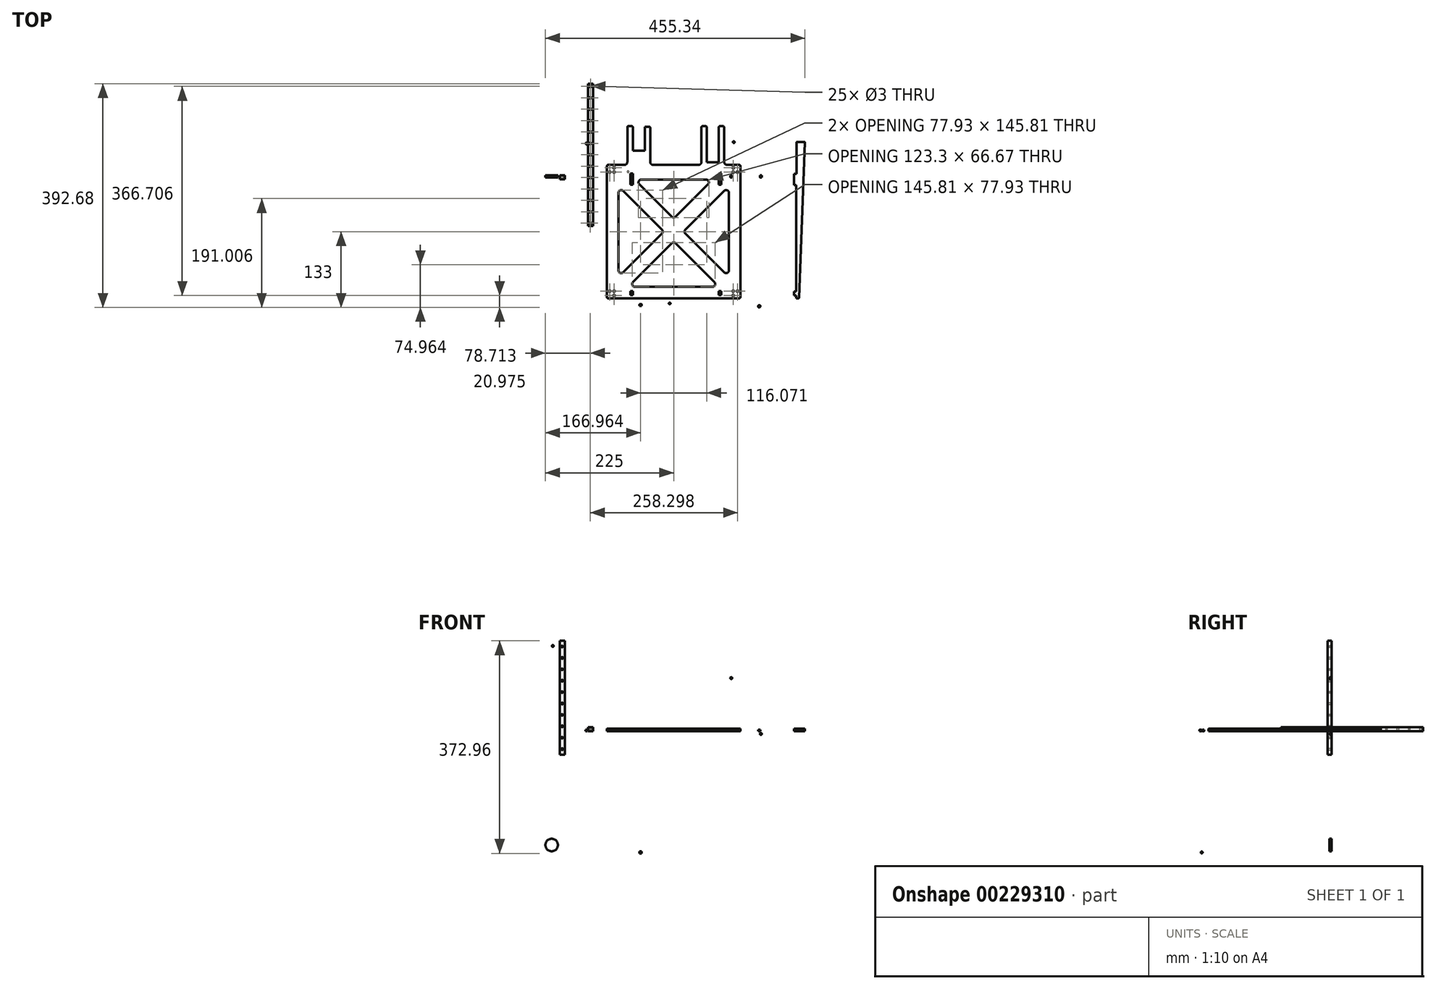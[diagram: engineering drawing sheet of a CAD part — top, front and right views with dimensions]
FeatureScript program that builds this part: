
annotation { "Feature Type Name" : "Feature", "Feature Type Description" : "" }
export const myFeature = defineFeature(function(context is Context, id is Id, definition is map)
    precondition{}
    {
        {
            var Q0;
            Q0=qCreatedBy(makeId("Top.planeOp"),FACE);
            var sketch = newSketch(context, id + "F0", { "sketchPlane" : qUnion([Q0])});
            skCircle(sketch, "E0", {"center": v(165.5, 58) * mm, "radius": 1.5 * mm});
            skCircle(sketch, "E1", {"center": v(-45.5, 91) * mm, "radius": 1.5 * mm});
            skCircle(sketch, "E2", {"center": v(210, 90) * mm, "radius": 2 * mm});
            skCircle(sketch, "E3", {"center": v(-93, 67) * mm, "radius": 1.5 * mm});
            skCircle(sketch, "E4", {"center": v(213, 67) * mm, "radius": 1.5 * mm});
            skCircle(sketch, "E5", {"center": v(210, 59) * mm, "radius": 2 * mm});
            skCircle(sketch, "E6", {"center": v(-81, -229) * mm, "radius": 2 * mm});
            skCircle(sketch, "E7", {"center": v(198, -220) * mm, "radius": 2 * mm});
            skCircle(sketch, "E8", {"center": v(-81, 78) * mm, "radius": 2 * mm});
            skCircle(sketch, "E9", {"center": v(198, 64) * mm, "radius": 2 * mm});
            skCircle(sketch, "E10", {"center": v(203, 47) * mm, "radius": 1.65 * mm});
            skCircle(sketch, "E11", {"center": v(203, 7) * mm, "radius": 1.65 * mm});
            skCircle(sketch, "E12", {"center": v(203, -173) * mm, "radius": 1.65 * mm});
            skCircle(sketch, "E13", {"center": v(-83, 47) * mm, "radius": 1.65 * mm});
            skCircle(sketch, "E14", {"center": v(-83, 7) * mm, "radius": 1.65 * mm});
            skCircle(sketch, "E15", {"center": v(-83, -173) * mm, "radius": 1.65 * mm});
            skCircle(sketch, "E16", {"center": v(-83, -193) * mm, "radius": 1.65 * mm});
            skCircle(sketch, "E17", {"center": v(-83, -153) * mm, "radius": 1.65 * mm});
            skCircle(sketch, "E18", {"center": v(-83, 27) * mm, "radius": 1.65 * mm});
            skCircle(sketch, "E19", {"center": v(203, -193) * mm, "radius": 1.65 * mm});
            skCircle(sketch, "E20", {"center": v(203, -153) * mm, "radius": 1.65 * mm});
            skCircle(sketch, "E21", {"center": v(203, 27) * mm, "radius": 1.65 * mm});
            skCircle(sketch, "E22", {"center": v(201, 78) * mm, "radius": 2 * mm});
            skCircle(sketch, "E23", {"center": v(-78, 64) * mm, "radius": 2 * mm});
            skCircle(sketch, "E24", {"center": v(201, -229) * mm, "radius": 2 * mm});
            skCircle(sketch, "E25", {"center": v(-78, -220) * mm, "radius": 2 * mm});
            skCircle(sketch, "E26", {"center": v(-90, 59) * mm, "radius": 2 * mm});
            skCircle(sketch, "E27", {"center": v(213, 81) * mm, "radius": 1.5 * mm});
            skCircle(sketch, "E28", {"center": v(-93, 81) * mm, "radius": 1.5 * mm});
            skCircle(sketch, "E29", {"center": v(-90, 90) * mm, "radius": 2 * mm});
            skCircle(sketch, "E30", {"center": v(-45.5, 58) * mm, "radius": 1.5 * mm});
            skCircle(sketch, "E31", {"center": v(165.5, 91) * mm, "radius": 1.5 * mm});
            skCircle(sketch, "E32", {"center": v(-93, -219) * mm, "radius": 1.5 * mm});
            skCircle(sketch, "E33", {"center": v(-93, -233) * mm, "radius": 1.5 * mm});
            skCircle(sketch, "E34", {"center": v(213, -233) * mm, "radius": 1.5 * mm});
            skCircle(sketch, "E35", {"center": v(213, -219) * mm, "radius": 1.5 * mm});
            skCircle(sketch, "E36", {"center": v(67, -225) * mm, "radius": 1.5 * mm});
            skCircle(sketch, "E37", {"center": v(53, -225) * mm, "radius": 1.5 * mm});
            skLineSegment(sketch, "E38", {"start": v(147.5, 57) * mm, "end": v(152.5, 57) * mm});
            skLineSegment(sketch, "E39", {"start": v(152.5, 61) * mm, "end": v(147.5, 61) * mm});
            skLineSegment(sketch, "E40", {"start": v(178.5, 88) * mm, "end": v(183.5, 88) * mm});
            skLineSegment(sketch, "E41", {"start": v(183.5, 92) * mm, "end": v(178.5, 92) * mm});
            skLineSegment(sketch, "E42", {"start": v(-58.5, 61) * mm, "end": v(-63.5, 61) * mm});
            skLineSegment(sketch, "E43", {"start": v(-63.5, 57) * mm, "end": v(-58.5, 57) * mm});
            skLineSegment(sketch, "E44", {"start": v(-27.5, 92) * mm, "end": v(-32.5, 92) * mm});
            skLineSegment(sketch, "E45", {"start": v(-32.5, 88) * mm, "end": v(-27.5, 88) * mm});
            skLineSegment(sketch, "E46", {"start": v(187, 49) * mm, "end": v(187, 53) * mm});
            skLineSegment(sketch, "E47", {"start": v(-67, 53) * mm, "end": v(-67, 49) * mm});
            skLineSegment(sketch, "E48", {"start": v(188, 95) * mm, "end": v(188, 91) * mm});
            skLineSegment(sketch, "E49", {"start": v(193, 86) * mm, "end": v(195, 86) * mm});
            skLineSegment(sketch, "E50", {"start": v(200, 91) * mm, "end": v(200, 95) * mm});
            skLineSegment(sketch, "E51", {"start": v(215, 96) * mm, "end": v(201, 96) * mm});
            skLineSegment(sketch, "E52", {"start": v(-80, 95) * mm, "end": v(-80, 91) * mm});
            skLineSegment(sketch, "E53", {"start": v(-75, 86) * mm, "end": v(-73, 86) * mm});
            skLineSegment(sketch, "E54", {"start": v(-68, 91) * mm, "end": v(-68, 95) * mm});
            skLineSegment(sketch, "E55", {"start": v(-58.5, 92) * mm, "end": v(-63.5, 92) * mm});
            skLineSegment(sketch, "E56", {"start": v(-63.5, 88) * mm, "end": v(-58.5, 88) * mm});
            skLineSegment(sketch, "E57", {"start": v(-27.5, 61) * mm, "end": v(-32.5, 61) * mm});
            skLineSegment(sketch, "E58", {"start": v(-32.5, 57) * mm, "end": v(-27.5, 57) * mm});
            skLineSegment(sketch, "E59", {"start": v(147.5, 88) * mm, "end": v(152.5, 88) * mm});
            skLineSegment(sketch, "E60", {"start": v(152.5, 92) * mm, "end": v(147.5, 92) * mm});
            skLineSegment(sketch, "E61", {"start": v(178.5, 57) * mm, "end": v(183.5, 57) * mm});
            skLineSegment(sketch, "E62", {"start": v(183.5, 61) * mm, "end": v(178.5, 61) * mm});
            skLineSegment(sketch, "E63", {"start": v(-81, 96) * mm, "end": v(-95, 96) * mm});
            skArc(sketch, "E64", {"start": v(152.5, 57) * mm, "mid": v(154.5, 59) * mm, "end": v(152.5, 61) * mm});
            skArc(sketch, "E65", {"start": v(147.5, 61) * mm, "mid": v(145.5, 59) * mm, "end": v(147.5, 57) * mm});
            skArc(sketch, "E66", {"start": v(183.5, 88) * mm, "mid": v(185.5, 90) * mm, "end": v(183.5, 92) * mm});
            skArc(sketch, "E67", {"start": v(178.5, 92) * mm, "mid": v(176.5, 90) * mm, "end": v(178.5, 88) * mm});
            skArc(sketch, "E68", {"start": v(-63.5, 61) * mm, "mid": v(-65.5, 59) * mm, "end": v(-63.5, 57) * mm});
            skArc(sketch, "E69", {"start": v(-58.5, 57) * mm, "mid": v(-56.5, 59) * mm, "end": v(-58.5, 61) * mm});
            skArc(sketch, "E70", {"start": v(-32.5, 92) * mm, "mid": v(-34.5, 90) * mm, "end": v(-32.5, 88) * mm});
            skArc(sketch, "E71", {"start": v(-27.5, 88) * mm, "mid": v(-25.5, 90) * mm, "end": v(-27.5, 92) * mm});
            skArc(sketch, "E72", {"start": v(195, 41) * mm, "mid": v(192.66, 46.66) * mm, "end": v(187, 49) * mm});
            skArc(sketch, "E73", {"start": v(-67, 49) * mm, "mid": v(-72.66, 46.66) * mm, "end": v(-75, 41) * mm});
            skArc(sketch, "E74", {"start": v(-75, -214) * mm, "mid": v(-72.66, -219.66) * mm, "end": v(-67, -222) * mm});
            skArc(sketch, "E75", {"start": v(187, -222) * mm, "mid": v(192.66, -219.66) * mm, "end": v(195, -214) * mm});
            skArc(sketch, "E76", {"start": v(188, 95) * mm, "mid": v(187.7, 95.7) * mm, "end": v(187, 96) * mm});
            skArc(sketch, "E77", {"start": v(188, 91) * mm, "mid": v(189.46, 87.46) * mm, "end": v(193, 86) * mm});
            skArc(sketch, "E78", {"start": v(195, 86) * mm, "mid": v(198.54, 87.46) * mm, "end": v(200, 91) * mm});
            skArc(sketch, "E79", {"start": v(201, 96) * mm, "mid": v(200.3, 95.7) * mm, "end": v(200, 95) * mm});
            skArc(sketch, "E80", {"start": v(216, 95) * mm, "mid": v(215.7, 95.7) * mm, "end": v(215, 96) * mm});
            skArc(sketch, "E81", {"start": v(215, -236) * mm, "mid": v(215.7, -235.7) * mm, "end": v(216, -235) * mm});
            skArc(sketch, "E82", {"start": v(-96, -235) * mm, "mid": v(-95.7, -235.7) * mm, "end": v(-95, -236) * mm});
            skArc(sketch, "E83", {"start": v(-95, 96) * mm, "mid": v(-95.7, 95.7) * mm, "end": v(-96, 95) * mm});
            skArc(sketch, "E84", {"start": v(-80, 95) * mm, "mid": v(-80.3, 95.7) * mm, "end": v(-81, 96) * mm});
            skArc(sketch, "E85", {"start": v(-80, 91) * mm, "mid": v(-78.54, 87.46) * mm, "end": v(-75, 86) * mm});
            skArc(sketch, "E86", {"start": v(-73, 86) * mm, "mid": v(-69.46, 87.46) * mm, "end": v(-68, 91) * mm});
            skArc(sketch, "E87", {"start": v(-67, 96) * mm, "mid": v(-67.7, 95.7) * mm, "end": v(-68, 95) * mm});
            skArc(sketch, "E88", {"start": v(-63.5, 92) * mm, "mid": v(-65.5, 90) * mm, "end": v(-63.5, 88) * mm});
            skArc(sketch, "E89", {"start": v(-58.5, 88) * mm, "mid": v(-56.5, 90) * mm, "end": v(-58.5, 92) * mm});
            skArc(sketch, "E90", {"start": v(-32.5, 61) * mm, "mid": v(-34.5, 59) * mm, "end": v(-32.5, 57) * mm});
            skArc(sketch, "E91", {"start": v(-27.5, 57) * mm, "mid": v(-25.5, 59) * mm, "end": v(-27.5, 61) * mm});
            skArc(sketch, "E92", {"start": v(152.5, 88) * mm, "mid": v(154.5, 90) * mm, "end": v(152.5, 92) * mm});
            skArc(sketch, "E93", {"start": v(147.5, 92) * mm, "mid": v(145.5, 90) * mm, "end": v(147.5, 88) * mm});
            skArc(sketch, "E94", {"start": v(183.5, 57) * mm, "mid": v(185.5, 59) * mm, "end": v(183.5, 61) * mm});
            skArc(sketch, "E95", {"start": v(178.5, 61) * mm, "mid": v(176.5, 59) * mm, "end": v(178.5, 57) * mm});
            skLineSegment(sketch, "E96", {"start": v(-67, 96) * mm, "end": v(187, 96) * mm});
            skLineSegment(sketch, "E97", {"start": v(-67, 53) * mm, "end": v(187, 53) * mm});
            skLineSegment(sketch, "E98", {"start": v(216, 95) * mm, "end": v(216, -235) * mm});
            skLineSegment(sketch, "E99", {"start": v(195, 41) * mm, "end": v(195, -214) * mm});
            skLineSegment(sketch, "E100", {"start": v(187, -222) * mm, "end": v(-67, -222) * mm});
            skLineSegment(sketch, "E101", {"start": v(215, -236) * mm, "end": v(-95, -236) * mm});
            skLineSegment(sketch, "E102", {"start": v(-96, -235) * mm, "end": v(-96, 95) * mm});
            skLineSegment(sketch, "E103", {"start": v(-75, 41) * mm, "end": v(-75, -214) * mm});
            skCircle(sketch, "E104", {"center": v(203, -133) * mm, "radius": 1.5 * mm});
            skCircle(sketch, "E105", {"center": v(203, -113) * mm, "radius": 1.5 * mm});
            skCircle(sketch, "E106", {"center": v(203, -93) * mm, "radius": 1.5 * mm});
            skCircle(sketch, "E107", {"center": v(203, -73) * mm, "radius": 1.5 * mm});
            skCircle(sketch, "E108", {"center": v(203, -53) * mm, "radius": 1.5 * mm});
            skCircle(sketch, "E109", {"center": v(203, -33) * mm, "radius": 1.5 * mm});
            skCircle(sketch, "E110", {"center": v(203, -13) * mm, "radius": 1.85 * mm});
            skCircle(sketch, "E111", {"center": v(-83, -113) * mm, "radius": 1.5 * mm});
            skCircle(sketch, "E112", {"center": v(-83, -133) * mm, "radius": 1.5 * mm});
            skCircle(sketch, "E113", {"center": v(-83, -93) * mm, "radius": 1.5 * mm});
            skCircle(sketch, "E114", {"center": v(-83, -73) * mm, "radius": 1.5 * mm});
            skCircle(sketch, "E115", {"center": v(-83, -53) * mm, "radius": 1.5 * mm});
            skCircle(sketch, "E116", {"center": v(-83, -33) * mm, "radius": 1.5 * mm});
            skCircle(sketch, "E117", {"center": v(-83, -13) * mm, "radius": 1.5 * mm});
            skSolve(sketch);
        }
        {
            var Q0;
            Q0=qCreatedBy(makeId("Top.planeOp"),FACE);
            var sketch = newSketch(context, id + "F1", { "sketchPlane" : qUnion([Q0])});
            skCircle(sketch, "E118", {"center": v(-20, 6.05) * mm, "radius": 1.5 * mm});
            skCircle(sketch, "E119", {"center": v(140, 6.05) * mm, "radius": 1.5 * mm});
            skCircle(sketch, "E120", {"center": v(195.5, 1) * mm, "radius": 1.65 * mm});
            skCircle(sketch, "E121", {"center": v(210.5, 11) * mm, "radius": 1.65 * mm});
            skCircle(sketch, "E122", {"center": v(180, 6) * mm, "radius": 1.5 * mm});
            skCircle(sketch, "E123", {"center": v(194, 18) * mm, "radius": 1.65 * mm});
            skCircle(sketch, "E124", {"center": v(194, -6) * mm, "radius": 1.65 * mm});
            skCircle(sketch, "E125", {"center": v(-92, -6) * mm, "radius": 1.65 * mm});
            skCircle(sketch, "E126", {"center": v(-92, 18) * mm, "radius": 1.65 * mm});
            skCircle(sketch, "E127", {"center": v(-40, 6) * mm, "radius": 1.5 * mm});
            skCircle(sketch, "E128", {"center": v(-78, 6) * mm, "radius": 1.5 * mm});
            skCircle(sketch, "E129", {"center": v(-90.5, 1) * mm, "radius": 1.65 * mm});
            skCircle(sketch, "E130", {"center": v(-75.5, 11) * mm, "radius": 1.65 * mm});
            skCircle(sketch, "E131", {"center": v(-75.5, 1) * mm, "radius": 1.65 * mm});
            skCircle(sketch, "E132", {"center": v(-90.5, 11) * mm, "radius": 1.65 * mm});
            skCircle(sketch, "E133", {"center": v(-60, 6) * mm, "radius": 1.5 * mm});
            skCircle(sketch, "E134", {"center": v(-74, 18) * mm, "radius": 1.65 * mm});
            skCircle(sketch, "E135", {"center": v(-74, -6) * mm, "radius": 1.65 * mm});
            skCircle(sketch, "E136", {"center": v(212, -6) * mm, "radius": 1.65 * mm});
            skCircle(sketch, "E137", {"center": v(212, 18) * mm, "radius": 1.65 * mm});
            skCircle(sketch, "E138", {"center": v(160, 6) * mm, "radius": 1.5 * mm});
            skCircle(sketch, "E139", {"center": v(198, 6) * mm, "radius": 1.5 * mm});
            skCircle(sketch, "E140", {"center": v(210.5, 1) * mm, "radius": 1.65 * mm});
            skCircle(sketch, "E141", {"center": v(195.5, 11) * mm, "radius": 1.65 * mm});
            skCircle(sketch, "E142", {"center": v(0, 6.05) * mm, "radius": 1.5 * mm});
            skLineSegment(sketch, "E143", {"start": v(193, -10) * mm, "end": v(213, -10) * mm});
            skLineSegment(sketch, "E144", {"start": v(191, -0.5) * mm, "end": v(191, -8) * mm});
            skLineSegment(sketch, "E145", {"start": v(-71, -8) * mm, "end": v(-71, -0.5) * mm});
            skLineSegment(sketch, "E146", {"start": v(-93, -10) * mm, "end": v(-73, -10) * mm});
            skLineSegment(sketch, "E147", {"start": v(-95, 20) * mm, "end": v(-95, -8) * mm});
            skLineSegment(sketch, "E148", {"start": v(-73, 22) * mm, "end": v(-93, 22) * mm});
            skLineSegment(sketch, "E149", {"start": v(-71, 12.5) * mm, "end": v(-71, 20) * mm});
            skLineSegment(sketch, "E150", {"start": v(191, 20) * mm, "end": v(191, 12.5) * mm});
            skLineSegment(sketch, "E151", {"start": v(213, 22) * mm, "end": v(193, 22) * mm});
            skLineSegment(sketch, "E152", {"start": v(215, -8) * mm, "end": v(215, 20) * mm});
            skArc(sketch, "E153", {"start": v(213, -10) * mm, "mid": v(214.41, -9.41) * mm, "end": v(215, -8) * mm});
            skArc(sketch, "E154", {"start": v(191, -8) * mm, "mid": v(191.59, -9.41) * mm, "end": v(193, -10) * mm});
            skArc(sketch, "E155", {"start": v(191, -0.5) * mm, "mid": v(190.41, 0.91) * mm, "end": v(189, 1.5) * mm});
            skArc(sketch, "E156", {"start": v(-69, 1.5) * mm, "mid": v(-70.41, 0.91) * mm, "end": v(-71, -0.5) * mm});
            skArc(sketch, "E157", {"start": v(-73, -10) * mm, "mid": v(-71.59, -9.41) * mm, "end": v(-71, -8) * mm});
            skArc(sketch, "E158", {"start": v(-95, -8) * mm, "mid": v(-94.41, -9.41) * mm, "end": v(-93, -10) * mm});
            skArc(sketch, "E159", {"start": v(-93, 22) * mm, "mid": v(-94.41, 21.41) * mm, "end": v(-95, 20) * mm});
            skArc(sketch, "E160", {"start": v(-71, 20) * mm, "mid": v(-71.59, 21.41) * mm, "end": v(-73, 22) * mm});
            skArc(sketch, "E161", {"start": v(-71, 12.5) * mm, "mid": v(-70.41, 11.09) * mm, "end": v(-69, 10.5) * mm});
            skArc(sketch, "E162", {"start": v(189, 10.5) * mm, "mid": v(190.41, 11.09) * mm, "end": v(191, 12.5) * mm});
            skArc(sketch, "E163", {"start": v(193, 22) * mm, "mid": v(191.59, 21.41) * mm, "end": v(191, 20) * mm});
            skArc(sketch, "E164", {"start": v(215, 20) * mm, "mid": v(214.41, 21.41) * mm, "end": v(213, 22) * mm});
            skLineSegment(sketch, "E165", {"start": v(-69, 10.5) * mm, "end": v(189, 10.5) * mm});
            skLineSegment(sketch, "E166", {"start": v(189, 1.5) * mm, "end": v(-69, 1.5) * mm});
            skCircle(sketch, "E167", {"center": v(20, 6.05) * mm, "radius": 1.5 * mm});
            skCircle(sketch, "E168", {"center": v(40, 6.05) * mm, "radius": 1.5 * mm});
            skCircle(sketch, "E169", {"center": v(60, 6.05) * mm, "radius": 1.5 * mm});
            skCircle(sketch, "E170", {"center": v(120, 6.05) * mm, "radius": 1.5 * mm});
            skCircle(sketch, "E171", {"center": v(80, 6.05) * mm, "radius": 1.5 * mm});
            skCircle(sketch, "E172", {"center": v(100, 6.05) * mm, "radius": 1.5 * mm});
            skSolve(sketch);
        }
        {
            var Q0;
            Q0=makeQuery(id+"F0.imprint","IMPRINT",FACE,{"disambiguationData":[TD([[makeQuery(id+"F0.imprint","IMPRINT",EDGE,{"derivedFrom":sQuery(id+"F0.wireOp",EDGE,"E0")}),1.0]])]});
            extrude(context, id + "F2", {"entities" : qUnion([Q0]), "depth" : 2 * mm});
        }
        {
            var Q0;
            Q0=makeQuery(id+"F1.imprint","IMPRINT",FACE,{"disambiguationData":[TD([[makeQuery(id+"F1.imprint","IMPRINT",EDGE,{"derivedFrom":sQuery(id+"F1.wireOp",EDGE,"E118")}),1.0]])]});
            extrude(context, id + "F3", {"entities" : qUnion([Q0]), "depth" : 2 * mm});
        }
        {
            var Q0;
            Q0=qCreatedBy(makeId("Top.planeOp"),FACE);
            var sketch = newSketch(context, id + "F4", { "sketchPlane" : qUnion([Q0])});
            skCircle(sketch, "E173", {"center": v(53, -225) * mm, "radius": 1.5 * mm});
            skCircle(sketch, "E174", {"center": v(-90, 59) * mm, "radius": 2 * mm});
            skCircle(sketch, "E175", {"center": v(-81, -229) * mm, "radius": 2 * mm});
            skCircle(sketch, "E176", {"center": v(198, -220) * mm, "radius": 2 * mm});
            skCircle(sketch, "E177", {"center": v(-81, 78) * mm, "radius": 2 * mm});
            skCircle(sketch, "E178", {"center": v(198, 64) * mm, "radius": 2 * mm});
            skCircle(sketch, "E179", {"center": v(75.5, 90) * mm, "radius": 2 * mm});
            skCircle(sketch, "E180", {"center": v(44.5, 59) * mm, "radius": 2 * mm});
            skCircle(sketch, "E181", {"center": v(75.5, 59) * mm, "radius": 2 * mm});
            skCircle(sketch, "E182", {"center": v(44.5, 90) * mm, "radius": 2 * mm});
            skCircle(sketch, "E183", {"center": v(60, 74.5) * mm, "radius": 11.75 * mm});
            skCircle(sketch, "E184", {"center": v(201, 78) * mm, "radius": 2 * mm});
            skCircle(sketch, "E185", {"center": v(-78, 64) * mm, "radius": 2 * mm});
            skCircle(sketch, "E186", {"center": v(201, -229) * mm, "radius": 2 * mm});
            skCircle(sketch, "E187", {"center": v(-78, -220) * mm, "radius": 2 * mm});
            skCircle(sketch, "E188", {"center": v(210, 59) * mm, "radius": 2 * mm});
            skCircle(sketch, "E189", {"center": v(67, -225) * mm, "radius": 1.5 * mm});
            skCircle(sketch, "E190", {"center": v(-93, -219) * mm, "radius": 1.5 * mm});
            skCircle(sketch, "E191", {"center": v(-93, -233) * mm, "radius": 1.5 * mm});
            skCircle(sketch, "E192", {"center": v(213, -233) * mm, "radius": 1.5 * mm});
            skCircle(sketch, "E193", {"center": v(213, -219) * mm, "radius": 1.5 * mm});
            skCircle(sketch, "E194", {"center": v(213, 81) * mm, "radius": 1.5 * mm});
            skCircle(sketch, "E195", {"center": v(213, 67) * mm, "radius": 1.5 * mm});
            skCircle(sketch, "E196", {"center": v(-93, 81) * mm, "radius": 1.5 * mm});
            skCircle(sketch, "E197", {"center": v(-93, 67) * mm, "radius": 1.5 * mm});
            skLineSegment(sketch, "E198", {"start": v(187, 49) * mm, "end": v(187, 53) * mm});
            skLineSegment(sketch, "E199", {"start": v(-67, 53) * mm, "end": v(-67, 49) * mm});
            skLineSegment(sketch, "E200", {"start": v(163, 62.75) * mm, "end": v(168, 62.75) * mm});
            skLineSegment(sketch, "E201", {"start": v(168, 86.25) * mm, "end": v(163, 86.25) * mm});
            skLineSegment(sketch, "E202", {"start": v(147.5, 88) * mm, "end": v(152.5, 88) * mm});
            skLineSegment(sketch, "E203", {"start": v(152.5, 92) * mm, "end": v(147.5, 92) * mm});
            skLineSegment(sketch, "E204", {"start": v(178.5, 57) * mm, "end": v(183.5, 57) * mm});
            skLineSegment(sketch, "E205", {"start": v(183.5, 61) * mm, "end": v(178.5, 61) * mm});
            skLineSegment(sketch, "E206", {"start": v(-27.5, 61) * mm, "end": v(-32.5, 61) * mm});
            skLineSegment(sketch, "E207", {"start": v(-32.5, 57) * mm, "end": v(-27.5, 57) * mm});
            skLineSegment(sketch, "E208", {"start": v(-58.5, 92) * mm, "end": v(-63.5, 92) * mm});
            skLineSegment(sketch, "E209", {"start": v(-63.5, 88) * mm, "end": v(-58.5, 88) * mm});
            skLineSegment(sketch, "E210", {"start": v(-84, 84) * mm, "end": v(-95, 84) * mm});
            skLineSegment(sketch, "E211", {"start": v(-84, 95) * mm, "end": v(-84, 84) * mm});
            skLineSegment(sketch, "E212", {"start": v(-80, 95) * mm, "end": v(-80, 91) * mm});
            skLineSegment(sketch, "E213", {"start": v(-75, 86) * mm, "end": v(-73, 86) * mm});
            skLineSegment(sketch, "E214", {"start": v(-68, 91) * mm, "end": v(-68, 95) * mm});
            skLineSegment(sketch, "E215", {"start": v(188, 95) * mm, "end": v(188, 91) * mm});
            skLineSegment(sketch, "E216", {"start": v(193, 86) * mm, "end": v(195, 86) * mm});
            skLineSegment(sketch, "E217", {"start": v(200, 91) * mm, "end": v(200, 95) * mm});
            skLineSegment(sketch, "E218", {"start": v(203, 96) * mm, "end": v(201, 96) * mm});
            skLineSegment(sketch, "E219", {"start": v(204, 84) * mm, "end": v(204, 95) * mm});
            skLineSegment(sketch, "E220", {"start": v(215, 84) * mm, "end": v(204, 84) * mm});
            skLineSegment(sketch, "E221", {"start": v(-43, 86.25) * mm, "end": v(-48, 86.25) * mm});
            skLineSegment(sketch, "E222", {"start": v(-48, 62.75) * mm, "end": v(-43, 62.75) * mm});
            skLineSegment(sketch, "E223", {"start": v(-27.5, 92) * mm, "end": v(-32.5, 92) * mm});
            skLineSegment(sketch, "E224", {"start": v(-32.5, 88) * mm, "end": v(-27.5, 88) * mm});
            skLineSegment(sketch, "E225", {"start": v(-58.5, 61) * mm, "end": v(-63.5, 61) * mm});
            skLineSegment(sketch, "E226", {"start": v(-63.5, 57) * mm, "end": v(-58.5, 57) * mm});
            skLineSegment(sketch, "E227", {"start": v(147.5, 57) * mm, "end": v(152.5, 57) * mm});
            skLineSegment(sketch, "E228", {"start": v(152.5, 61) * mm, "end": v(147.5, 61) * mm});
            skLineSegment(sketch, "E229", {"start": v(178.5, 88) * mm, "end": v(183.5, 88) * mm});
            skLineSegment(sketch, "E230", {"start": v(183.5, 92) * mm, "end": v(178.5, 92) * mm});
            skLineSegment(sketch, "E231", {"start": v(-81, 96) * mm, "end": v(-83, 96) * mm});
            skArc(sketch, "E232", {"start": v(195, 41) * mm, "mid": v(192.66, 46.66) * mm, "end": v(187, 49) * mm});
            skArc(sketch, "E233", {"start": v(-67, 49) * mm, "mid": v(-72.66, 46.66) * mm, "end": v(-75, 41) * mm});
            skArc(sketch, "E234", {"start": v(-75, -214) * mm, "mid": v(-72.66, -219.66) * mm, "end": v(-67, -222) * mm});
            skArc(sketch, "E235", {"start": v(187, -222) * mm, "mid": v(192.66, -219.66) * mm, "end": v(195, -214) * mm});
            skArc(sketch, "E236", {"start": v(168, 62.75) * mm, "mid": v(179.75, 74.5) * mm, "end": v(168, 86.25) * mm});
            skArc(sketch, "E237", {"start": v(163, 86.25) * mm, "mid": v(151.25, 74.5) * mm, "end": v(163, 62.75) * mm});
            skArc(sketch, "E238", {"start": v(152.5, 88) * mm, "mid": v(154.5, 90) * mm, "end": v(152.5, 92) * mm});
            skArc(sketch, "E239", {"start": v(147.5, 92) * mm, "mid": v(145.5, 90) * mm, "end": v(147.5, 88) * mm});
            skArc(sketch, "E240", {"start": v(183.5, 57) * mm, "mid": v(185.5, 59) * mm, "end": v(183.5, 61) * mm});
            skArc(sketch, "E241", {"start": v(178.5, 61) * mm, "mid": v(176.5, 59) * mm, "end": v(178.5, 57) * mm});
            skArc(sketch, "E242", {"start": v(-32.5, 61) * mm, "mid": v(-34.5, 59) * mm, "end": v(-32.5, 57) * mm});
            skArc(sketch, "E243", {"start": v(-27.5, 57) * mm, "mid": v(-25.5, 59) * mm, "end": v(-27.5, 61) * mm});
            skArc(sketch, "E244", {"start": v(-63.5, 92) * mm, "mid": v(-65.5, 90) * mm, "end": v(-63.5, 88) * mm});
            skArc(sketch, "E245", {"start": v(-58.5, 88) * mm, "mid": v(-56.5, 90) * mm, "end": v(-58.5, 92) * mm});
            skArc(sketch, "E246", {"start": v(-95, 84) * mm, "mid": v(-95.7, 83.7) * mm, "end": v(-96, 83) * mm});
            skArc(sketch, "E247", {"start": v(-83, 96) * mm, "mid": v(-83.7, 95.7) * mm, "end": v(-84, 95) * mm});
            skArc(sketch, "E248", {"start": v(-80, 95) * mm, "mid": v(-80.3, 95.7) * mm, "end": v(-81, 96) * mm});
            skArc(sketch, "E249", {"start": v(-80, 91) * mm, "mid": v(-78.54, 87.46) * mm, "end": v(-75, 86) * mm});
            skArc(sketch, "E250", {"start": v(-73, 86) * mm, "mid": v(-69.46, 87.46) * mm, "end": v(-68, 91) * mm});
            skArc(sketch, "E251", {"start": v(-67, 96) * mm, "mid": v(-67.7, 95.7) * mm, "end": v(-68, 95) * mm});
            skArc(sketch, "E252", {"start": v(188, 95) * mm, "mid": v(187.7, 95.7) * mm, "end": v(187, 96) * mm});
            skArc(sketch, "E253", {"start": v(188, 91) * mm, "mid": v(189.46, 87.46) * mm, "end": v(193, 86) * mm});
            skArc(sketch, "E254", {"start": v(195, 86) * mm, "mid": v(198.54, 87.46) * mm, "end": v(200, 91) * mm});
            skArc(sketch, "E255", {"start": v(201, 96) * mm, "mid": v(200.3, 95.7) * mm, "end": v(200, 95) * mm});
            skArc(sketch, "E256", {"start": v(204, 95) * mm, "mid": v(203.7, 95.7) * mm, "end": v(203, 96) * mm});
            skArc(sketch, "E257", {"start": v(216, 83) * mm, "mid": v(215.7, 83.7) * mm, "end": v(215, 84) * mm});
            skArc(sketch, "E258", {"start": v(215, -236) * mm, "mid": v(215.7, -235.7) * mm, "end": v(216, -235) * mm});
            skArc(sketch, "E259", {"start": v(-96, -235) * mm, "mid": v(-95.7, -235.7) * mm, "end": v(-95, -236) * mm});
            skArc(sketch, "E260", {"start": v(-48, 86.25) * mm, "mid": v(-59.75, 74.5) * mm, "end": v(-48, 62.75) * mm});
            skArc(sketch, "E261", {"start": v(-43, 62.75) * mm, "mid": v(-31.25, 74.5) * mm, "end": v(-43, 86.25) * mm});
            skArc(sketch, "E262", {"start": v(-32.5, 92) * mm, "mid": v(-34.5, 90) * mm, "end": v(-32.5, 88) * mm});
            skArc(sketch, "E263", {"start": v(-27.5, 88) * mm, "mid": v(-25.5, 90) * mm, "end": v(-27.5, 92) * mm});
            skArc(sketch, "E264", {"start": v(-63.5, 61) * mm, "mid": v(-65.5, 59) * mm, "end": v(-63.5, 57) * mm});
            skArc(sketch, "E265", {"start": v(-58.5, 57) * mm, "mid": v(-56.5, 59) * mm, "end": v(-58.5, 61) * mm});
            skArc(sketch, "E266", {"start": v(152.5, 57) * mm, "mid": v(154.5, 59) * mm, "end": v(152.5, 61) * mm});
            skArc(sketch, "E267", {"start": v(147.5, 61) * mm, "mid": v(145.5, 59) * mm, "end": v(147.5, 57) * mm});
            skArc(sketch, "E268", {"start": v(183.5, 88) * mm, "mid": v(185.5, 90) * mm, "end": v(183.5, 92) * mm});
            skArc(sketch, "E269", {"start": v(178.5, 92) * mm, "mid": v(176.5, 90) * mm, "end": v(178.5, 88) * mm});
            skLineSegment(sketch, "E270", {"start": v(-67, 96) * mm, "end": v(187, 96) * mm});
            skLineSegment(sketch, "E271", {"start": v(216, 83) * mm, "end": v(216, -235) * mm});
            skLineSegment(sketch, "E272", {"start": v(215, -236) * mm, "end": v(-95, -236) * mm});
            skLineSegment(sketch, "E273", {"start": v(-96, -235) * mm, "end": v(-96, 83) * mm});
            skLineSegment(sketch, "E274", {"start": v(-67, 53) * mm, "end": v(187, 53) * mm});
            skLineSegment(sketch, "E275", {"start": v(-75, 41) * mm, "end": v(-75, -214) * mm});
            skLineSegment(sketch, "E276", {"start": v(-67, -222) * mm, "end": v(187, -222) * mm});
            skLineSegment(sketch, "E277", {"start": v(195, -214) * mm, "end": v(195, 41) * mm});
            skSolve(sketch);
        }
        {
            var Q0;
            Q0=makeQuery(id+"F4.imprint","IMPRINT",FACE,{"disambiguationData":[TD([[makeQuery(id+"F4.imprint","IMPRINT",EDGE,{"derivedFrom":sQuery(id+"F4.wireOp",EDGE,"E173")}),1.0]])]});
            extrude(context, id + "F5", {"entities" : qUnion([Q0]), "depth" : 2 * mm});
        }
        {
            var Q0;
            Q0=qCreatedBy(makeId("Right.planeOp"),FACE);
            var sketch = newSketch(context, id + "F6", { "sketchPlane" : qUnion([Q0])});
            skCircle(sketch, "E278", {"center": v(-228, -213) * mm, "radius": 1.65 * mm});
            skCircle(sketch, "E279", {"center": v(37, -213) * mm, "radius": 1.65 * mm});
            skCircle(sketch, "E280", {"center": v(88, -189) * mm, "radius": 1.65 * mm});
            skCircle(sketch, "E281", {"center": v(88, 27) * mm, "radius": 1.65 * mm});
            skCircle(sketch, "E282", {"center": v(72, 93) * mm, "radius": 1.65 * mm});
            skCircle(sketch, "E283", {"center": v(-228, 69) * mm, "radius": 1.65 * mm});
            skCircle(sketch, "E284", {"center": v(-228, 93) * mm, "radius": 1.65 * mm});
            skCircle(sketch, "E285", {"center": v(72, 69) * mm, "radius": 1.65 * mm});
            skCircle(sketch, "E286", {"center": v(57, 27) * mm, "radius": 1.65 * mm});
            skCircle(sketch, "E287", {"center": v(57, -189) * mm, "radius": 1.65 * mm});
            skCircle(sketch, "E288", {"center": v(37, -189) * mm, "radius": 1.65 * mm});
            skCircle(sketch, "E289", {"center": v(-228, -189) * mm, "radius": 1.65 * mm});
            skLineSegment(sketch, "E290", {"start": v(-238, -182) * mm, "end": v(-238, -220) * mm});
            skLineSegment(sketch, "E291", {"start": v(-238, 100) * mm, "end": v(-238, 62) * mm});
            skArc(sketch, "E292", {"start": v(27, -182) * mm, "mid": v(41.14, -176.14) * mm, "end": v(47, -162) * mm});
            skArc(sketch, "E293", {"start": v(47, 42) * mm, "mid": v(41.14, 56.14) * mm, "end": v(27, 62) * mm});
            skLineSegment(sketch, "E294", {"start": v(-238, 100) * mm, "end": v(98, 100) * mm});
            skLineSegment(sketch, "E295", {"start": v(-238, 62) * mm, "end": v(27, 62) * mm});
            skLineSegment(sketch, "E296", {"start": v(27, -182) * mm, "end": v(-238, -182) * mm});
            skLineSegment(sketch, "E297", {"start": v(-238, -220) * mm, "end": v(98, -220) * mm});
            skLineSegment(sketch, "E298", {"start": v(47, 42) * mm, "end": v(47, -162) * mm});
            skLineSegment(sketch, "E299", {"start": v(98, 100) * mm, "end": v(98, -220) * mm});
            skSolve(sketch);
        }
        {
            var Q0;
            Q0=makeQuery(id+"F6.imprint","IMPRINT",FACE,{"disambiguationData":[TD([[makeQuery(id+"F6.imprint","IMPRINT",EDGE,{"derivedFrom":sQuery(id+"F6.wireOp",EDGE,"E278")}),1.0]])]});
            extrude(context, id + "F7", {"entities" : qUnion([Q0]), "depth" : 4 * mm});
        }
        {
            var Q0;
            Q0=qCreatedBy(makeId("Front.planeOp"),FACE);
            var sketch = newSketch(context, id + "F8", { "sketchPlane" : qUnion([Q0])});
            skCircle(sketch, "E300", {"center": v(213, -5) * mm, "radius": 1.65 * mm});
            skCircle(sketch, "E301", {"center": v(-93, -5) * mm, "radius": 1.65 * mm});
            skCircle(sketch, "E302", {"center": v(-93, 5) * mm, "radius": 1.65 * mm});
            skCircle(sketch, "E303", {"center": v(213, 5) * mm, "radius": 1.65 * mm});
            skLineSegment(sketch, "E304", {"start": v(220, -19) * mm, "end": v(220, 19) * mm});
            skLineSegment(sketch, "E305", {"start": v(-100, 19) * mm, "end": v(-100, -19) * mm});
            skLineSegment(sketch, "E306", {"start": v(-100, -19) * mm, "end": v(220, -19) * mm});
            skLineSegment(sketch, "E307", {"start": v(220, 19) * mm, "end": v(-100, 19) * mm});
            skSolve(sketch);
        }
        {
            var Q0;
            Q0=makeQuery(id+"F8.imprint","IMPRINT",FACE,{"disambiguationData":[TD([[makeQuery(id+"F8.imprint","IMPRINT",EDGE,{"derivedFrom":sQuery(id+"F8.wireOp",EDGE,"E300")}),1.0]])]});
            extrude(context, id + "F9", {"entities" : qUnion([Q0]), "depth" : 4 * mm});
        }
        {
            var Q0;
            Q0=qCreatedBy(makeId("Front.planeOp"),FACE);
            var sketch = newSketch(context, id + "F10", { "sketchPlane" : qUnion([Q0])});
            skCircle(sketch, "E308", {"center": v(-154, -200) * mm, "radius": 11 * mm});
            skCircle(sketch, "E309", {"center": v(-170.5, 94) * mm, "radius": 1.65 * mm});
            skCircle(sketch, "E310", {"center": v(40.5, 94) * mm, "radius": 1.65 * mm});
            skCircle(sketch, "E311", {"center": v(-210, 22) * mm, "radius": 1.65 * mm});
            skCircle(sketch, "E312", {"center": v(90, -58) * mm, "radius": 1.65 * mm});
            skCircle(sketch, "E313", {"center": v(40, -30) * mm, "radius": 2 * mm});
            skCircle(sketch, "E314", {"center": v(71, 1) * mm, "radius": 2 * mm});
            skCircle(sketch, "E315", {"center": v(55.5, -14.5) * mm, "radius": 11.5 * mm});
            skCircle(sketch, "E316", {"center": v(40, 1) * mm, "radius": 2 * mm});
            skCircle(sketch, "E317", {"center": v(71, -30) * mm, "radius": 2 * mm});
            skCircle(sketch, "E318", {"center": v(90, 22) * mm, "radius": 1.65 * mm});
            skCircle(sketch, "E319", {"center": v(-210, -58) * mm, "radius": 1.65 * mm});
            skCircle(sketch, "E320", {"center": v(50.5, 94) * mm, "radius": 1.65 * mm});
            skCircle(sketch, "E321", {"center": v(-160.5, 94) * mm, "radius": 1.65 * mm});
            skCircle(sketch, "E322", {"center": v(-182.25, -200) * mm, "radius": 5.5 * mm});
            skLineSegment(sketch, "E323", {"start": v(-216, 100) * mm, "end": v(96, 100) * mm});
            skLineSegment(sketch, "E324", {"start": v(96, -220) * mm, "end": v(-216, -220) * mm});
            skLineSegment(sketch, "E325", {"start": v(-216, 100) * mm, "end": v(-216, -220) * mm});
            skLineSegment(sketch, "E326", {"start": v(96, -220) * mm, "end": v(96, 100) * mm});
            skCircle(sketch, "E327", {"center": v(-210, -178) * mm, "radius": 1.65 * mm});
            skCircle(sketch, "E328", {"center": v(90, -178) * mm, "radius": 1.65 * mm});
            skSolve(sketch);
        }
        {
            var Q0;
            Q0=makeQuery(id+"F10.imprint","IMPRINT",FACE,{"disambiguationData":[TD([[makeQuery(id+"F10.imprint","IMPRINT",EDGE,{"derivedFrom":sQuery(id+"F10.wireOp",EDGE,"E308")}),1.0]])]});
            extrude(context, id + "F11", {"entities" : qUnion([Q0]), "depth" : 4 * mm});
        }
        {
            var Q0;
            Q0=qCreatedBy(makeId("Front.planeOp"),FACE);
            var sketch = newSketch(context, id + "F12", { "sketchPlane" : qUnion([Q0])});
            skCircle(sketch, "E329", {"center": v(161, 93) * mm, "radius": 1.65 * mm});
            skCircle(sketch, "E330", {"center": v(-40, 93) * mm, "radius": 1.65 * mm});
            skCircle(sketch, "E331", {"center": v(210.5, -158) * mm, "radius": 1.65 * mm});
            skCircle(sketch, "E332", {"center": v(-89.5, -158) * mm, "radius": 1.65 * mm});
            skCircle(sketch, "E333", {"center": v(12, 24) * mm, "radius": 1 * mm});
            skCircle(sketch, "E334", {"center": v(-21, -158) * mm, "radius": 1 * mm});
            skCircle(sketch, "E335", {"center": v(12, -158) * mm, "radius": 1 * mm});
            skCircle(sketch, "E336", {"center": v(-21, 24) * mm, "radius": 1 * mm});
            skCircle(sketch, "E337", {"center": v(-89.5, 36) * mm, "radius": 1.65 * mm});
            skCircle(sketch, "E338", {"center": v(210.5, 36) * mm, "radius": 1.65 * mm});
            skCircle(sketch, "E339", {"center": v(-50, 93) * mm, "radius": 1.65 * mm});
            skCircle(sketch, "E340", {"center": v(171, 93) * mm, "radius": 1.65 * mm});
            skLineSegment(sketch, "E341", {"start": v(204.5, -206) * mm, "end": v(204.5, -219) * mm});
            skLineSegment(sketch, "E342", {"start": v(157, -191) * mm, "end": v(189.5, -191) * mm});
            skLineSegment(sketch, "E343", {"start": v(142, -219) * mm, "end": v(142, -206) * mm});
            skLineSegment(sketch, "E344", {"start": v(-21, -206) * mm, "end": v(-21, -219) * mm});
            skLineSegment(sketch, "E345", {"start": v(-68.5, -191) * mm, "end": v(-36, -191) * mm});
            skLineSegment(sketch, "E346", {"start": v(-83.5, -219) * mm, "end": v(-83.5, -206) * mm});
            skLineSegment(sketch, "E347", {"start": v(-83.5, -219) * mm, "end": v(-95.5, -219) * mm});
            skLineSegment(sketch, "E348", {"start": v(-66.5, 61) * mm, "end": v(-95.5, 61) * mm});
            skLineSegment(sketch, "E349", {"start": v(-66.5, 99) * mm, "end": v(-66.5, 61) * mm});
            skLineSegment(sketch, "E350", {"start": v(187.5, 61) * mm, "end": v(187.5, 99) * mm});
            skLineSegment(sketch, "E351", {"start": v(216.5, 61) * mm, "end": v(187.5, 61) * mm});
            skLineSegment(sketch, "E352", {"start": v(216.5, -219) * mm, "end": v(204.5, -219) * mm});
            skLineSegment(sketch, "E353", {"start": v(-9, 19) * mm, "end": v(-23, 19) * mm});
            skLineSegment(sketch, "E354", {"start": v(-23, -153) * mm, "end": v(-9, -153) * mm});
            skLineSegment(sketch, "E355", {"start": v(-9, -153) * mm, "end": v(-9, -167) * mm});
            skLineSegment(sketch, "E356", {"start": v(-9, -167) * mm, "end": v(0, -167) * mm});
            skLineSegment(sketch, "E357", {"start": v(0, -167) * mm, "end": v(0, -153) * mm});
            skLineSegment(sketch, "E358", {"start": v(0, -153) * mm, "end": v(14, -153) * mm});
            skLineSegment(sketch, "E359", {"start": v(14, 19) * mm, "end": v(0, 19) * mm});
            skLineSegment(sketch, "E360", {"start": v(0, 19) * mm, "end": v(0, 33) * mm});
            skLineSegment(sketch, "E361", {"start": v(0, 33) * mm, "end": v(-9, 33) * mm});
            skLineSegment(sketch, "E362", {"start": v(-9, 33) * mm, "end": v(-9, 19) * mm});
            skLineSegment(sketch, "E363", {"start": v(73, -206) * mm, "end": v(48, -206) * mm});
            skLineSegment(sketch, "E364", {"start": v(48, -216) * mm, "end": v(73, -216) * mm});
            skArc(sketch, "E365", {"start": v(204.5, -206) * mm, "mid": v(200.1, -195.4) * mm, "end": v(189.5, -191) * mm});
            skArc(sketch, "E366", {"start": v(157, -191) * mm, "mid": v(146.4, -195.4) * mm, "end": v(142, -206) * mm});
            skArc(sketch, "E367", {"start": v(-21, -206) * mm, "mid": v(-25.4, -195.4) * mm, "end": v(-36, -191) * mm});
            skArc(sketch, "E368", {"start": v(-68.5, -191) * mm, "mid": v(-79.1, -195.4) * mm, "end": v(-83.5, -206) * mm});
            skArc(sketch, "E369", {"start": v(-23, 19) * mm, "mid": v(-25.12, 18.12) * mm, "end": v(-26, 16) * mm});
            skArc(sketch, "E370", {"start": v(-26, -150) * mm, "mid": v(-25.12, -152.12) * mm, "end": v(-23, -153) * mm});
            skArc(sketch, "E371", {"start": v(14, -153) * mm, "mid": v(16.12, -152.12) * mm, "end": v(17, -150) * mm});
            skArc(sketch, "E372", {"start": v(17, 16) * mm, "mid": v(16.12, 18.12) * mm, "end": v(14, 19) * mm});
            skArc(sketch, "E373", {"start": v(48, -206) * mm, "mid": v(43, -211) * mm, "end": v(48, -216) * mm});
            skArc(sketch, "E374", {"start": v(73, -216) * mm, "mid": v(78, -211) * mm, "end": v(73, -206) * mm});
            skLineSegment(sketch, "E375", {"start": v(187.5, 99) * mm, "end": v(-66.5, 99) * mm});
            skLineSegment(sketch, "E376", {"start": v(142, -219) * mm, "end": v(-21, -219) * mm});
            skLineSegment(sketch, "E377", {"start": v(-26, 16) * mm, "end": v(-26, -150) * mm});
            skLineSegment(sketch, "E378", {"start": v(17, 16) * mm, "end": v(17, -150) * mm});
            skCircle(sketch, "E379", {"center": v(142, 24) * mm, "radius": 1 * mm});
            skCircle(sketch, "E380", {"center": v(109, -158) * mm, "radius": 1 * mm});
            skCircle(sketch, "E381", {"center": v(142, -158) * mm, "radius": 1 * mm});
            skCircle(sketch, "E382", {"center": v(109, 24) * mm, "radius": 1 * mm});
            skLineSegment(sketch, "E383", {"start": v(121, 19) * mm, "end": v(107, 19) * mm});
            skLineSegment(sketch, "E384", {"start": v(107, -153) * mm, "end": v(121, -153) * mm});
            skLineSegment(sketch, "E385", {"start": v(121, -153) * mm, "end": v(121, -167) * mm});
            skLineSegment(sketch, "E386", {"start": v(121, -167) * mm, "end": v(130, -167) * mm});
            skLineSegment(sketch, "E387", {"start": v(130, -167) * mm, "end": v(130, -153) * mm});
            skLineSegment(sketch, "E388", {"start": v(130, -153) * mm, "end": v(144, -153) * mm});
            skLineSegment(sketch, "E389", {"start": v(144, 19) * mm, "end": v(130, 19) * mm});
            skLineSegment(sketch, "E390", {"start": v(130, 19) * mm, "end": v(130, 33) * mm});
            skLineSegment(sketch, "E391", {"start": v(130, 33) * mm, "end": v(121, 33) * mm});
            skLineSegment(sketch, "E392", {"start": v(121, 33) * mm, "end": v(121, 19) * mm});
            skArc(sketch, "E393", {"start": v(107, 19) * mm, "mid": v(104.88, 18.12) * mm, "end": v(104, 16) * mm});
            skArc(sketch, "E394", {"start": v(104, -150) * mm, "mid": v(104.88, -152.12) * mm, "end": v(107, -153) * mm});
            skArc(sketch, "E395", {"start": v(144, -153) * mm, "mid": v(146.12, -152.12) * mm, "end": v(147, -150) * mm});
            skArc(sketch, "E396", {"start": v(147, 16) * mm, "mid": v(146.12, 18.12) * mm, "end": v(144, 19) * mm});
            skLineSegment(sketch, "E397", {"start": v(104, 16) * mm, "end": v(104, -150) * mm});
            skLineSegment(sketch, "E398", {"start": v(147, 16) * mm, "end": v(147, -150) * mm});
            skLineSegment(sketch, "E399", {"start": v(-95.5, 61) * mm, "end": v(-95.5, -219) * mm});
            skLineSegment(sketch, "E400", {"start": v(216.5, -219) * mm, "end": v(216.5, 61) * mm});
            skSolve(sketch);
        }
        {
            var Q0;
            Q0=makeQuery(id+"F12.imprint","IMPRINT",FACE,{"disambiguationData":[TD([[makeQuery(id+"F12.imprint","IMPRINT",EDGE,{"derivedFrom":sQuery(id+"F12.wireOp",EDGE,"E329")}),1.0]])]});
            extrude(context, id + "F13", {"entities" : qUnion([Q0]), "depth" : 4 * mm});
        }
        {
            var Q0;
            Q0=qCreatedBy(makeId("Top.planeOp"),FACE);
            var sketch = newSketch(context, id + "F14", { "sketchPlane" : qUnion([Q0])});
            skLineSegment(sketch, "E401.bottom", {"start": v(-90.49, 160.68) * mm, "end": v(-81.49, 160.68) * mm});
            skLineSegment(sketch, "E401.top", {"start": v(-90.49, -89.32) * mm, "end": v(-81.49, -89.32) * mm});
            skLineSegment(sketch, "E401.left", {"start": v(-90.49, 160.68) * mm, "end": v(-90.49, -89.32) * mm});
            skLineSegment(sketch, "E401.right", {"start": v(-81.49, 160.68) * mm, "end": v(-81.49, -89.32) * mm});
            skCircle(sketch, "E402", {"center": v(-85.99, 155.68) * mm, "radius": 1.5 * mm});
            skPoint(sketch, "E402.centerSnap0", {"position": v(-85.99, 160.68) * mm});
            skCircle(sketch, "E403", {"center": v(-85.99, 135.68) * mm, "radius": 1.5 * mm});
            skCircle(sketch, "E404", {"center": v(-85.99, 115.68) * mm, "radius": 1.5 * mm});
            skCircle(sketch, "E405", {"center": v(-85.99, 95.68) * mm, "radius": 1.5 * mm});
            skCircle(sketch, "E406", {"center": v(-85.99, 75.68) * mm, "radius": 1.5 * mm});
            skCircle(sketch, "E407", {"center": v(-85.99, 55.68) * mm, "radius": 1.5 * mm});
            skCircle(sketch, "E408", {"center": v(-85.99, 35.68) * mm, "radius": 1.5 * mm});
            skCircle(sketch, "E409", {"center": v(-85.99, 15.68) * mm, "radius": 1.5 * mm});
            skCircle(sketch, "E410", {"center": v(-85.99, -4.32) * mm, "radius": 1.5 * mm});
            skCircle(sketch, "E411", {"center": v(-85.99, -24.32) * mm, "radius": 1.5 * mm});
            skCircle(sketch, "E412", {"center": v(-85.99, -44.32) * mm, "radius": 1.5 * mm});
            skCircle(sketch, "E413", {"center": v(-85.99, -64.32) * mm, "radius": 1.5 * mm});
            skCircle(sketch, "E414", {"center": v(-86.29, -84.32) * mm, "radius": 1.5 * mm});
            skSolve(sketch);
        }
        {
            var Q0;
            Q0=makeQuery(id+"F14.imprint","IMPRINT",FACE,{"disambiguationData":[TD([[makeQuery(id+"F14.imprint","IMPRINT",EDGE,{"derivedFrom":sQuery(id+"F14.wireOp",EDGE,"E401.bottom")}),-1.0]])]});
            extrude(context, id + "F15", {"entities" : qUnion([Q0]), "depth" : 7 * mm});
        }
        {
            var Q0;
            Q0=qCreatedBy(makeId("Front.planeOp"),FACE);
            var sketch = newSketch(context, id + "F16", { "sketchPlane" : qUnion([Q0])});
            skLineSegment(sketch, "E415.bottom", {"start": v(-140.02, 158.31) * mm, "end": v(-131.02, 158.31) * mm});
            skLineSegment(sketch, "E415.top", {"start": v(-140.02, -41.69) * mm, "end": v(-131.02, -41.69) * mm});
            skLineSegment(sketch, "E415.left", {"start": v(-140.02, 158.31) * mm, "end": v(-140.02, -41.69) * mm});
            skLineSegment(sketch, "E415.right", {"start": v(-131.02, 158.31) * mm, "end": v(-131.02, -41.69) * mm});
            skCircle(sketch, "E416", {"center": v(-135.52, 148.31) * mm, "radius": 1.5 * mm});
            skPoint(sketch, "E416.centerSnap0", {"position": v(-135.52, 158.31) * mm});
            skCircle(sketch, "E417", {"center": v(-135.52, 128.31) * mm, "radius": 1.5 * mm});
            skCircle(sketch, "E418", {"center": v(-135.52, 108.31) * mm, "radius": 1.5 * mm});
            skCircle(sketch, "E419", {"center": v(-135.52, 88.31) * mm, "radius": 1.5 * mm});
            skCircle(sketch, "E420", {"center": v(-135.52, 68.31) * mm, "radius": 1.5 * mm});
            skCircle(sketch, "E421", {"center": v(-135.52, 48.31) * mm, "radius": 1.5 * mm});
            skCircle(sketch, "E422", {"center": v(-135.52, 28.31) * mm, "radius": 1.5 * mm});
            skCircle(sketch, "E423", {"center": v(-135.52, 8.31) * mm, "radius": 1.5 * mm});
            skCircle(sketch, "E424", {"center": v(-135.52, -11.69) * mm, "radius": 1.5 * mm});
            skCircle(sketch, "E425", {"center": v(-135.52, -31.69) * mm, "radius": 1.5 * mm});
            skSolve(sketch);
        }
        {
            var Q0;
            Q0=makeQuery(id+"F16.imprint","IMPRINT",FACE,{"disambiguationData":[TD([[makeQuery(id+"F16.imprint","IMPRINT",EDGE,{"derivedFrom":sQuery(id+"F16.wireOp",EDGE,"E415.bottom")}),-1.0]])]});
            extrude(context, id + "F17", {"entities" : qUnion([Q0]), "depth" : 7 * mm});
        }
        {
            var Q0;
            Q0=qCreatedBy(makeId("Front.planeOp"),FACE);
            var sketch = newSketch(context, id + "F18", { "sketchPlane" : qUnion([Q0])});
            skCircle(sketch, "E426", {"center": v(-152.05, 149.31) * mm, "radius": 1.5 * mm});
            skCircle(sketch, "E427", {"center": v(-119.05, 149.31) * mm, "radius": 1.5 * mm});
            skCircle(sketch, "E428", {"center": v(-119.05, -32.69) * mm, "radius": 1.5 * mm});
            skCircle(sketch, "E429", {"center": v(-152.05, -32.69) * mm, "radius": 1.5 * mm});
            skLineSegment(sketch, "E430", {"start": v(-142.05, -27.69) * mm, "end": v(-155.05, -27.69) * mm});
            skLineSegment(sketch, "E431", {"start": v(-155.05, 144.31) * mm, "end": v(-142.05, 144.31) * mm});
            skLineSegment(sketch, "E432", {"start": v(-157.05, 152.31) * mm, "end": v(-157.05, 146.31) * mm});
            skLineSegment(sketch, "E433", {"start": v(-116.05, 154.31) * mm, "end": v(-155.05, 154.31) * mm});
            skLineSegment(sketch, "E434", {"start": v(-114.05, 146.31) * mm, "end": v(-114.05, 152.31) * mm});
            skLineSegment(sketch, "E435", {"start": v(-129.05, 144.31) * mm, "end": v(-116.05, 144.31) * mm});
            skLineSegment(sketch, "E436", {"start": v(-116.05, -27.69) * mm, "end": v(-129.05, -27.69) * mm});
            skLineSegment(sketch, "E437", {"start": v(-114.05, -35.69) * mm, "end": v(-114.05, -29.69) * mm});
            skLineSegment(sketch, "E438", {"start": v(-155.05, -37.69) * mm, "end": v(-116.05, -37.69) * mm});
            skLineSegment(sketch, "E439", {"start": v(-157.05, -29.69) * mm, "end": v(-157.05, -35.69) * mm});
            skArc(sketch, "E440", {"start": v(-155.05, -27.69) * mm, "mid": v(-156.46, -28.28) * mm, "end": v(-157.05, -29.69) * mm});
            skArc(sketch, "E441", {"start": v(-142.05, -27.69) * mm, "mid": v(-140.64, -27.1) * mm, "end": v(-140.05, -25.69) * mm});
            skArc(sketch, "E442", {"start": v(-140.05, 142.31) * mm, "mid": v(-140.64, 143.72) * mm, "end": v(-142.05, 144.31) * mm});
            skArc(sketch, "E443", {"start": v(-157.05, 146.31) * mm, "mid": v(-156.46, 144.9) * mm, "end": v(-155.05, 144.31) * mm});
            skArc(sketch, "E444", {"start": v(-155.05, 154.31) * mm, "mid": v(-156.46, 153.72) * mm, "end": v(-157.05, 152.31) * mm});
            skArc(sketch, "E445", {"start": v(-114.05, 152.31) * mm, "mid": v(-114.64, 153.72) * mm, "end": v(-116.05, 154.31) * mm});
            skArc(sketch, "E446", {"start": v(-116.05, 144.31) * mm, "mid": v(-114.64, 144.9) * mm, "end": v(-114.05, 146.31) * mm});
            skArc(sketch, "E447", {"start": v(-129.05, 144.31) * mm, "mid": v(-130.46, 143.72) * mm, "end": v(-131.05, 142.31) * mm});
            skArc(sketch, "E448", {"start": v(-131.05, -25.69) * mm, "mid": v(-130.46, -27.1) * mm, "end": v(-129.05, -27.69) * mm});
            skArc(sketch, "E449", {"start": v(-114.05, -29.69) * mm, "mid": v(-114.64, -28.28) * mm, "end": v(-116.05, -27.69) * mm});
            skArc(sketch, "E450", {"start": v(-116.05, -37.69) * mm, "mid": v(-114.64, -37.1) * mm, "end": v(-114.05, -35.69) * mm});
            skArc(sketch, "E451", {"start": v(-157.05, -35.69) * mm, "mid": v(-156.46, -37.1) * mm, "end": v(-155.05, -37.69) * mm});
            skCircle(sketch, "E452", {"center": v(-135.55, 148.31) * mm, "radius": 1.5 * mm});
            skCircle(sketch, "E453", {"center": v(-135.55, 128.31) * mm, "radius": 1.5 * mm});
            skCircle(sketch, "E454", {"center": v(-135.55, 108.31) * mm, "radius": 1.5 * mm});
            skCircle(sketch, "E455", {"center": v(-135.55, 88.31) * mm, "radius": 1.5 * mm});
            skCircle(sketch, "E456", {"center": v(-135.55, 68.31) * mm, "radius": 1.5 * mm});
            skCircle(sketch, "E457", {"center": v(-135.55, 48.31) * mm, "radius": 1.5 * mm});
            skCircle(sketch, "E458", {"center": v(-135.55, 28.31) * mm, "radius": 1.5 * mm});
            skCircle(sketch, "E459", {"center": v(-135.55, 8.31) * mm, "radius": 1.5 * mm});
            skCircle(sketch, "E460", {"center": v(-135.55, -11.69) * mm, "radius": 1.5 * mm});
            skCircle(sketch, "E461", {"center": v(-135.55, -31.69) * mm, "radius": 1.5 * mm});
            skLineSegment(sketch, "E462", {"start": v(-140.05, 142.31) * mm, "end": v(-140.05, -25.69) * mm});
            skLineSegment(sketch, "E463", {"start": v(-131.05, -25.69) * mm, "end": v(-131.05, 142.31) * mm});
            skSolve(sketch);
        }
        {
            var Q0;
            Q0=qCreatedBy(makeId("Top.planeOp"),FACE);
            var sketch = newSketch(context, id + "F19", { "sketchPlane" : qUnion([Q0])});
            skLineSegment(sketch, "E464.bottom", {"start": v(-47, 8) * mm, "end": v(167, 8) * mm});
            skLineSegment(sketch, "E464.top", {"start": v(-47, -206) * mm, "end": v(167, -206) * mm});
            skLineSegment(sketch, "E464.left", {"start": v(-47, 8) * mm, "end": v(-47, -206) * mm});
            skLineSegment(sketch, "E464.right", {"start": v(167, 8) * mm, "end": v(167, -206) * mm});
            skCircle(sketch, "E465", {"center": v(164.5, 5.5) * mm, "radius": 1.5 * mm});
            skCircle(sketch, "E466", {"center": v(-44.5, 5.5) * mm, "radius": 1.5 * mm});
            skCircle(sketch, "E467", {"center": v(164.5, -203.5) * mm, "radius": 1.5 * mm});
            skCircle(sketch, "E468", {"center": v(-44.5, -203.5) * mm, "radius": 1.5 * mm});
            skSolve(sketch);
        }
        {
            var Q0;
            Q0=qCreatedBy(makeId("Top.planeOp"),FACE);
            var sketch = newSketch(context, id + "F20", { "sketchPlane" : qUnion([Q0])});
            skLineSegment(sketch, "E469.top", {"start": v(-11.66, 42.8) * mm, "end": v(9.34, 42.8) * mm});
            skLineSegment(sketch, "E469.left", {"start": v(-11.66, 53.3) * mm, "end": v(-11.66, 42.8) * mm});
            skLineSegment(sketch, "E469.right", {"start": v(9.34, 53.3) * mm, "end": v(9.34, 42.8) * mm});
            skCircle(sketch, "E470", {"center": v(60.04, 74.5) * mm, "radius": 6.5 * mm});
            skCircle(sketch, "E471", {"center": v(50.54, 74.5) * mm, "radius": 1.5 * mm});
            skCircle(sketch, "E472", {"center": v(69.54, 74.5) * mm, "radius": 1.5 * mm});
            skCircle(sketch, "E473", {"center": v(60.04, 65) * mm, "radius": 1.5 * mm});
            skCircle(sketch, "E474", {"center": v(60.04, 84) * mm, "radius": 1.5 * mm});
            skLineSegment(sketch, "E475.top", {"start": v(118.2, 22.5) * mm, "end": v(139.2, 22.5) * mm});
            skLineSegment(sketch, "E475.left", {"start": v(118.2, 33) * mm, "end": v(118.2, 22.5) * mm});
            skLineSegment(sketch, "E475.right", {"start": v(139.2, 33) * mm, "end": v(139.2, 22.5) * mm});
            skLineSegment(sketch, "E476", {"start": v(18.84, 83.16) * mm, "end": v(18.84, 23) * mm});
            skLineSegment(sketch, "E477", {"start": v(23.84, 18) * mm, "end": v(103.7, 18) * mm});
            skLineSegment(sketch, "E478", {"start": v(108.7, 23) * mm, "end": v(108.7, 83.94) * mm});
            skLineSegment(sketch, "E479", {"start": v(148.7, 83.92) * mm, "end": v(148.7, 23) * mm});
            skLineSegment(sketch, "E480", {"start": v(153.7, 18) * mm, "end": v(175, 18) * mm});
            skLineSegment(sketch, "E481", {"start": v(177, 16) * mm, "end": v(177, -214) * mm});
            skLineSegment(sketch, "E482", {"start": v(175, -216) * mm, "end": v(-55, -216) * mm});
            skLineSegment(sketch, "E483", {"start": v(-21.3, 84) * mm, "end": v(-21.3, 23) * mm});
            skLineSegment(sketch, "E484", {"start": v(-57, -214) * mm, "end": v(-57, 16) * mm});
            skLineSegment(sketch, "E485", {"start": v(-55, 18) * mm, "end": v(-26.3, 18) * mm});
            skCircle(sketch, "E486", {"center": v(164.5, 5.47) * mm, "radius": 1.5 * mm});
            skCircle(sketch, "E487", {"center": v(-44.5, 5.5) * mm, "radius": 1.5 * mm});
            skCircle(sketch, "E488", {"center": v(164.51, -203.53) * mm, "radius": 1.5 * mm});
            skCircle(sketch, "E489", {"center": v(-44.49, -203.5) * mm, "radius": 1.5 * mm});
            skCircle(sketch, "E490", {"center": v(164.5, 13) * mm, "radius": 1.5 * mm});
            skCircle(sketch, "E491", {"center": v(172.01, 5.47) * mm, "radius": 1.5 * mm});
            skCircle(sketch, "E492", {"center": v(-52, 5.5) * mm, "radius": 1.5 * mm});
            skCircle(sketch, "E493", {"center": v(-44.5, 13) * mm, "radius": 1.5 * mm});
            skCircle(sketch, "E494", {"center": v(172.01, -203.53) * mm, "radius": 1.5 * mm});
            skCircle(sketch, "E495", {"center": v(-52, -203.53) * mm, "radius": 1.5 * mm});
            skCircle(sketch, "E496", {"center": v(-44.49, -211.03) * mm, "radius": 1.5 * mm});
            skCircle(sketch, "E497", {"center": v(164.51, -211.03) * mm, "radius": 1.5 * mm});
            skLineSegment(sketch, "E498", {"start": v(-7.93, -196) * mm, "end": v(127.93, -196) * mm});
            skLineSegment(sketch, "E499", {"start": v(131.46, -187.46) * mm, "end": v(63.54, -119.54) * mm});
            skPoint(sketch, "E499.endSnap0", {"position": v(60, -196) * mm});
            skLineSegment(sketch, "E500", {"start": v(56.46, -119.54) * mm, "end": v(-11.46, -187.46) * mm});
            skLineSegment(sketch, "E501.bottom", {"start": v(-11.66, 3) * mm, "end": v(-15.66, 3) * mm});
            skLineSegment(sketch, "E501.top", {"start": v(-11.66, -17) * mm, "end": v(-15.66, -17) * mm});
            skLineSegment(sketch, "E501.left", {"start": v(-11.66, 3) * mm, "end": v(-11.66, -17) * mm});
            skLineSegment(sketch, "E501.right", {"start": v(-15.66, 3) * mm, "end": v(-15.66, -17) * mm});
            skLineSegment(sketch, "E502", {"start": v(-37, -31.07) * mm, "end": v(-37, -166.93) * mm});
            skLineSegment(sketch, "E503", {"start": v(-28.46, -170.46) * mm, "end": v(39.46, -102.54) * mm});
            skPoint(sketch, "E503.endSnap0", {"position": v(-37, -99) * mm});
            skLineSegment(sketch, "E504", {"start": v(39.46, -95.46) * mm, "end": v(-28.46, -27.54) * mm});
            skLineSegment(sketch, "E505", {"start": v(157, -31.07) * mm, "end": v(157, -166.93) * mm});
            skLineSegment(sketch, "E506", {"start": v(148.46, -170.46) * mm, "end": v(80.54, -102.54) * mm});
            skPoint(sketch, "E506.endSnap0", {"position": v(157, -99) * mm});
            skLineSegment(sketch, "E507", {"start": v(80.54, -95.46) * mm, "end": v(148.46, -27.54) * mm});
            skLineSegment(sketch, "E508", {"start": v(-0.2, -16.2) * mm, "end": v(56.46, -72.87) * mm});
            skLineSegment(sketch, "E509", {"start": v(63.54, -72.87) * mm, "end": v(120.2, -16.2) * mm});
            skLineSegment(sketch, "E510", {"start": v(116.67, -7.66) * mm, "end": v(3.33, -7.66) * mm});
            skLineSegment(sketch, "E511", {"start": v(-11.66, 53.3) * mm, "end": v(-11.66, 84) * mm});
            skLineSegment(sketch, "E512", {"start": v(-13.66, 86) * mm, "end": v(-19.3, 86) * mm});
            skLineSegment(sketch, "E513", {"start": v(9.34, 53.3) * mm, "end": v(9.34, 85.16) * mm});
            skLineSegment(sketch, "E514", {"start": v(9.34, 85.16) * mm, "end": v(16.84, 85.16) * mm});
            skLineSegment(sketch, "E515", {"start": v(118.2, 33) * mm, "end": v(118.2, 83.98) * mm});
            skLineSegment(sketch, "E516", {"start": v(110.68, 85.94) * mm, "end": v(116.18, 85.98) * mm});
            skLineSegment(sketch, "E517", {"start": v(139.2, 33) * mm, "end": v(139.2, 83.92) * mm});
            skLineSegment(sketch, "E518", {"start": v(141.2, 85.92) * mm, "end": v(146.7, 85.92) * mm});
            skLineSegment(sketch, "E519.bottom", {"start": v(139.2, 3) * mm, "end": v(143.2, 3) * mm});
            skLineSegment(sketch, "E519.top", {"start": v(139.2, -17) * mm, "end": v(143.2, -17) * mm});
            skLineSegment(sketch, "E519.left", {"start": v(139.2, 3) * mm, "end": v(139.2, -17) * mm});
            skLineSegment(sketch, "E519.right", {"start": v(143.2, 3) * mm, "end": v(143.2, -17) * mm});
            skLineSegment(sketch, "E520.bottom", {"start": v(-11.66, -203.5) * mm, "end": v(-15.66, -203.5) * mm});
            skLineSegment(sketch, "E520.top", {"start": v(-11.66, -210.5) * mm, "end": v(-15.66, -210.5) * mm});
            skLineSegment(sketch, "E520.left", {"start": v(-11.66, -203.5) * mm, "end": v(-11.66, -210.5) * mm});
            skLineSegment(sketch, "E520.right", {"start": v(-15.66, -203.5) * mm, "end": v(-15.66, -210.5) * mm});
            skLineSegment(sketch, "E521.bottom", {"start": v(139.2, -203.5) * mm, "end": v(143.2, -203.5) * mm});
            skLineSegment(sketch, "E521.top", {"start": v(139.2, -210.5) * mm, "end": v(143.2, -210.5) * mm});
            skLineSegment(sketch, "E521.left", {"start": v(139.2, -203.5) * mm, "end": v(139.2, -210.5) * mm});
            skLineSegment(sketch, "E521.right", {"start": v(143.2, -203.5) * mm, "end": v(143.2, -210.5) * mm});
            skPoint(sketch, "E522.visualSharp", {"position": v(-57, 18) * mm});
            skArc(sketch, "E522.filletArc", {"start": v(-55, 18) * mm, "mid": v(-56.41, 17.41) * mm, "end": v(-57, 16) * mm});
            skPoint(sketch, "E523.visualSharp", {"position": v(-57, -216) * mm});
            skArc(sketch, "E523.filletArc", {"start": v(-57, -214) * mm, "mid": v(-56.41, -215.41) * mm, "end": v(-55, -216) * mm});
            skPoint(sketch, "E524.visualSharp", {"position": v(177, -216) * mm});
            skArc(sketch, "E524.filletArc", {"start": v(175, -216) * mm, "mid": v(176.41, -215.41) * mm, "end": v(177, -214) * mm});
            skPoint(sketch, "E525.visualSharp", {"position": v(177, 18) * mm});
            skArc(sketch, "E525.filletArc", {"start": v(177, 16) * mm, "mid": v(176.41, 17.41) * mm, "end": v(175, 18) * mm});
            skPoint(sketch, "E526.visualSharp", {"position": v(-21.3, 86) * mm});
            skArc(sketch, "E526.filletArc", {"start": v(-19.3, 86) * mm, "mid": v(-20.72, 85.41) * mm, "end": v(-21.3, 84) * mm});
            skPoint(sketch, "E527.visualSharp", {"position": v(-11.66, 86) * mm});
            skArc(sketch, "E527.filletArc", {"start": v(-11.66, 84) * mm, "mid": v(-12.24, 85.41) * mm, "end": v(-13.66, 86) * mm});
            skPoint(sketch, "E528.visualSharp", {"position": v(18.84, 85.16) * mm});
            skArc(sketch, "E528.filletArc", {"start": v(18.84, 83.16) * mm, "mid": v(18.26, 84.57) * mm, "end": v(16.84, 85.16) * mm});
            skPoint(sketch, "E529.visualSharp", {"position": v(108.7, 85.92) * mm});
            skArc(sketch, "E529.filletArc", {"start": v(110.68, 85.94) * mm, "mid": v(109.28, 85.35) * mm, "end": v(108.7, 83.94) * mm});
            skPoint(sketch, "E530.visualSharp", {"position": v(118.2, 86) * mm});
            skArc(sketch, "E530.filletArc", {"start": v(118.2, 83.98) * mm, "mid": v(117.6, 85.4) * mm, "end": v(116.18, 85.98) * mm});
            skPoint(sketch, "E531.visualSharp", {"position": v(139.2, 85.92) * mm});
            skArc(sketch, "E531.filletArc", {"start": v(141.2, 85.92) * mm, "mid": v(139.79, 85.34) * mm, "end": v(139.2, 83.92) * mm});
            skPoint(sketch, "E532.visualSharp", {"position": v(148.7, 85.92) * mm});
            skArc(sketch, "E532.filletArc", {"start": v(148.7, 83.92) * mm, "mid": v(148.11, 85.34) * mm, "end": v(146.7, 85.92) * mm});
            skPoint(sketch, "E533.visualSharp", {"position": v(-21.3, 18) * mm});
            skArc(sketch, "E533.filletArc", {"start": v(-26.3, 18) * mm, "mid": v(-22.77, 19.46) * mm, "end": v(-21.3, 23) * mm});
            skPoint(sketch, "E534.visualSharp", {"position": v(18.84, 18) * mm});
            skArc(sketch, "E534.filletArc", {"start": v(18.84, 23) * mm, "mid": v(20.3, 19.46) * mm, "end": v(23.84, 18) * mm});
            skPoint(sketch, "E535.visualSharp", {"position": v(108.7, 18) * mm});
            skArc(sketch, "E535.filletArc", {"start": v(103.7, 18) * mm, "mid": v(107.24, 19.46) * mm, "end": v(108.7, 23) * mm});
            skPoint(sketch, "E536.visualSharp", {"position": v(148.7, 18) * mm});
            skArc(sketch, "E536.filletArc", {"start": v(148.7, 23) * mm, "mid": v(150.16, 19.46) * mm, "end": v(153.7, 18) * mm});
            skPoint(sketch, "E537.visualSharp", {"position": v(-8.75, -7.66) * mm});
            skArc(sketch, "E537.filletArc", {"start": v(3.33, -7.66) * mm, "mid": v(-1.3, -10.74) * mm, "end": v(-0.2, -16.2) * mm});
            skPoint(sketch, "E538.visualSharp", {"position": v(60, -76.4) * mm});
            skArc(sketch, "E538.filletArc", {"start": v(56.46, -72.87) * mm, "mid": v(60, -74.33) * mm, "end": v(63.54, -72.87) * mm});
            skPoint(sketch, "E539.visualSharp", {"position": v(157, -19) * mm});
            skArc(sketch, "E539.filletArc", {"start": v(157, -31.07) * mm, "mid": v(153.91, -26.45) * mm, "end": v(148.46, -27.54) * mm});
            skPoint(sketch, "E540.visualSharp", {"position": v(128.75, -7.66) * mm});
            skArc(sketch, "E540.filletArc", {"start": v(120.2, -16.2) * mm, "mid": v(121.3, -10.74) * mm, "end": v(116.67, -7.66) * mm});
            skPoint(sketch, "E541.visualSharp", {"position": v(77, -99) * mm});
            skArc(sketch, "E541.filletArc", {"start": v(80.54, -95.46) * mm, "mid": v(79.07, -99) * mm, "end": v(80.54, -102.54) * mm});
            skPoint(sketch, "E542.visualSharp", {"position": v(43, -99) * mm});
            skArc(sketch, "E542.filletArc", {"start": v(39.46, -102.54) * mm, "mid": v(40.93, -99) * mm, "end": v(39.46, -95.46) * mm});
            skPoint(sketch, "E543.visualSharp", {"position": v(-37, -19) * mm});
            skArc(sketch, "E543.filletArc", {"start": v(-28.46, -27.54) * mm, "mid": v(-33.91, -26.45) * mm, "end": v(-37, -31.07) * mm});
            skPoint(sketch, "E544.visualSharp", {"position": v(-37, -179) * mm});
            skArc(sketch, "E544.filletArc", {"start": v(-37, -166.93) * mm, "mid": v(-33.91, -171.55) * mm, "end": v(-28.46, -170.46) * mm});
            skPoint(sketch, "E545.visualSharp", {"position": v(-20, -196) * mm});
            skArc(sketch, "E545.filletArc", {"start": v(-11.46, -187.46) * mm, "mid": v(-12.55, -192.91) * mm, "end": v(-7.93, -196) * mm});
            skPoint(sketch, "E546.visualSharp", {"position": v(140, -196) * mm});
            skArc(sketch, "E546.filletArc", {"start": v(127.93, -196) * mm, "mid": v(132.55, -192.91) * mm, "end": v(131.46, -187.46) * mm});
            skPoint(sketch, "E547.visualSharp", {"position": v(157, -179) * mm});
            skArc(sketch, "E547.filletArc", {"start": v(148.46, -170.46) * mm, "mid": v(153.91, -171.55) * mm, "end": v(157, -166.93) * mm});
            skPoint(sketch, "E548.visualSharp", {"position": v(60, -116) * mm});
            skArc(sketch, "E548.filletArc", {"start": v(63.54, -119.54) * mm, "mid": v(60, -118.07) * mm, "end": v(56.46, -119.54) * mm});
            skLineSegment(sketch, "E549.bottom", {"start": v(270.97, -211.04) * mm, "end": v(274.97, -211.04) * mm});
            skLineSegment(sketch, "E549.top", {"start": v(270.97, -204.04) * mm, "end": v(274.96, -204.04) * mm});
            skLineSegment(sketch, "E549.left", {"start": v(270.97, -211.04) * mm, "end": v(270.97, -204.04) * mm});
            skLineSegment(sketch, "E550.bottom", {"start": v(274.96, -17.54) * mm, "end": v(270.97, -17.54) * mm});
            skLineSegment(sketch, "E550.top", {"start": v(275.38, 2.46) * mm, "end": v(270.97, 2.46) * mm});
            skLineSegment(sketch, "E550.right", {"start": v(270.97, -17.54) * mm, "end": v(270.97, 2.46) * mm});
            skLineSegment(sketch, "E551", {"start": v(274.96, -204.04) * mm, "end": v(274.96, -17.54) * mm});
            skLineSegment(sketch, "E552", {"start": v(275.38, 2.46) * mm, "end": v(275.38, 57.46) * mm});
            skPoint(sketch, "E552.endSnap0", {"position": v(139.2, 58.46) * mm});
            skLineSegment(sketch, "E553", {"start": v(276.38, 58.46) * mm, "end": v(289.34, 58.46) * mm});
            skLineSegment(sketch, "E554", {"start": v(274.97, -211.04) * mm, "end": v(274.97, -216.04) * mm});
            skLineSegment(sketch, "E555", {"start": v(274.97, -216.04) * mm, "end": v(279, -216.04) * mm});
            skLineSegment(sketch, "E556", {"start": v(280, -215.08) * mm, "end": v(290.34, 57.42) * mm});
            skPoint(sketch, "E557.visualSharp", {"position": v(279.97, -216.04) * mm});
            skArc(sketch, "E557.filletArc", {"start": v(279, -216.04) * mm, "mid": v(279.7, -215.76) * mm, "end": v(280, -215.08) * mm});
            skPoint(sketch, "E558.visualSharp", {"position": v(290.38, 58.46) * mm});
            skArc(sketch, "E558.filletArc", {"start": v(290.34, 57.42) * mm, "mid": v(290.06, 58.16) * mm, "end": v(289.34, 58.46) * mm});
            skPoint(sketch, "E559.visualSharp", {"position": v(275.38, 58.46) * mm});
            skArc(sketch, "E559.filletArc", {"start": v(276.38, 58.46) * mm, "mid": v(275.68, 58.17) * mm, "end": v(275.38, 57.46) * mm});
            skSolve(sketch);
        }
        {
            var Q0;
            Q0=makeQuery(id+"F20.imprint","IMPRINT",FACE,{"disambiguationData":[TD([[makeQuery(id+"F20.imprint","IMPRINT",EDGE,{"derivedFrom":sQuery(id+"F20.wireOp",EDGE,"E469.top")}),-1.0]])]});
            extrude(context, id + "F21", {"entities" : qUnion([Q0]), "depth" : 4 * mm});
        }
        {
            var Q0;
            Q0=makeQuery(id+"F18.imprint","IMPRINT",FACE,{"disambiguationData":[TD([[makeQuery(id+"F18.imprint","IMPRINT",EDGE,{"derivedFrom":sQuery(id+"F18.wireOp",EDGE,"E426")}),1.0]])]});
            extrude(context, id + "F22", {"entities" : qUnion([Q0]), "depth" : 2 * mm});
        }
        {
            var Q0;
            Q0=qCreatedBy(makeId("Top.planeOp"),FACE);
            var sketch = newSketch(context, id + "F23", { "sketchPlane" : qUnion([Q0])});
            skCircle(sketch, "E560", {"center": v(210, -230) * mm, "radius": 2 * mm});
            skCircle(sketch, "E561", {"center": v(-90, -230) * mm, "radius": 2 * mm});
            skCircle(sketch, "E562", {"center": v(-93, -172) * mm, "radius": 1.5 * mm});
            skCircle(sketch, "E563", {"center": v(213, -186) * mm, "radius": 1.5 * mm});
            skCircle(sketch, "E564", {"center": v(213, 79) * mm, "radius": 1.5 * mm});
            skCircle(sketch, "E565", {"center": v(-93, 79) * mm, "radius": 1.5 * mm});
            skCircle(sketch, "E566", {"center": v(-93, 93) * mm, "radius": 1.5 * mm});
            skCircle(sketch, "E567", {"center": v(213, 93) * mm, "radius": 1.5 * mm});
            skCircle(sketch, "E568", {"center": v(213, -172) * mm, "radius": 1.5 * mm});
            skCircle(sketch, "E569", {"center": v(-93, -186) * mm, "radius": 1.5 * mm});
            skCircle(sketch, "E570", {"center": v(-90, -199) * mm, "radius": 2 * mm});
            skCircle(sketch, "E571", {"center": v(210, -199) * mm, "radius": 2 * mm});
            skCircle(sketch, "E572", {"center": v(-66, 81) * mm, "radius": 1.6 * mm});
            skCircle(sketch, "E573", {"center": v(186, 81) * mm, "radius": 1.6 * mm});
            skCircle(sketch, "E574", {"center": v(66, -81) * mm, "radius": 1.6 * mm});
            skCircle(sketch, "E575", {"center": v(-66, -81) * mm, "radius": 1.6 * mm});
            skCircle(sketch, "E576", {"center": v(20, 53) * mm, "radius": 1 * mm});
            skCircle(sketch, "E577", {"center": v(201, 53) * mm, "radius": 1 * mm});
            skCircle(sketch, "E578", {"center": v(201, -174.5) * mm, "radius": 1 * mm});
            skCircle(sketch, "E579", {"center": v(201, -184) * mm, "radius": 1 * mm});
            skCircle(sketch, "E580", {"center": v(20, -44) * mm, "radius": 1 * mm});
            skCircle(sketch, "E581", {"center": v(20, -34.5) * mm, "radius": 1 * mm});
            skCircle(sketch, "E582", {"center": v(-62.5, 48) * mm, "radius": 1 * mm});
            skCircle(sketch, "E583", {"center": v(-13.5, 48) * mm, "radius": 1 * mm});
            skCircle(sketch, "E584", {"center": v(-13.5, -10) * mm, "radius": 1 * mm});
            skCircle(sketch, "E585", {"center": v(-62.5, -10) * mm, "radius": 1 * mm});
            skCircle(sketch, "E586", {"center": v(62.5, -10) * mm, "radius": 1 * mm});
            skCircle(sketch, "E587", {"center": v(13.5, -10) * mm, "radius": 1 * mm});
            skCircle(sketch, "E588", {"center": v(13.5, 48) * mm, "radius": 1 * mm});
            skCircle(sketch, "E589", {"center": v(62.5, 48) * mm, "radius": 1 * mm});
            skCircle(sketch, "E590", {"center": v(-20, -34.5) * mm, "radius": 1 * mm});
            skCircle(sketch, "E591", {"center": v(-20, -44) * mm, "radius": 1 * mm});
            skCircle(sketch, "E592", {"center": v(-81, -44) * mm, "radius": 1 * mm});
            skCircle(sketch, "E593", {"center": v(-81, -34.5) * mm, "radius": 1 * mm});
            skCircle(sketch, "E594", {"center": v(-81, 53) * mm, "radius": 1 * mm});
            skCircle(sketch, "E595", {"center": v(-20, 53) * mm, "radius": 1 * mm});
            skLineSegment(sketch, "E596", {"start": v(-78.5, -87.5) * mm, "end": v(-73.5, -87.5) * mm});
            skLineSegment(sketch, "E597", {"start": v(-73.5, -84.5) * mm, "end": v(-78.5, -84.5) * mm});
            skLineSegment(sketch, "E598", {"start": v(191.5, -87.5) * mm, "end": v(196.5, -87.5) * mm});
            skLineSegment(sketch, "E599", {"start": v(196.5, -84.5) * mm, "end": v(191.5, -84.5) * mm});
            skLineSegment(sketch, "E600", {"start": v(11.5, -87.5) * mm, "end": v(16.5, -87.5) * mm});
            skLineSegment(sketch, "E601", {"start": v(16.5, -84.5) * mm, "end": v(11.5, -84.5) * mm});
            skLineSegment(sketch, "E602", {"start": v(-48.5, -87.5) * mm, "end": v(-43.5, -87.5) * mm});
            skLineSegment(sketch, "E603", {"start": v(-43.5, -84.5) * mm, "end": v(-48.5, -84.5) * mm});
            skLineSegment(sketch, "E604", {"start": v(41.5, -77.5) * mm, "end": v(46.5, -77.5) * mm});
            skLineSegment(sketch, "E605", {"start": v(46.5, -74.5) * mm, "end": v(41.5, -74.5) * mm});
            skLineSegment(sketch, "E606", {"start": v(-18.5, -77.5) * mm, "end": v(-13.5, -77.5) * mm});
            skLineSegment(sketch, "E607", {"start": v(-13.5, -74.5) * mm, "end": v(-18.5, -74.5) * mm});
            skLineSegment(sketch, "E608", {"start": v(191.5, -67.5) * mm, "end": v(196.5, -67.5) * mm});
            skLineSegment(sketch, "E609", {"start": v(196.5, -64.5) * mm, "end": v(191.5, -64.5) * mm});
            skLineSegment(sketch, "E610", {"start": v(11.5, -67.5) * mm, "end": v(16.5, -67.5) * mm});
            skLineSegment(sketch, "E611", {"start": v(16.5, -64.5) * mm, "end": v(11.5, -64.5) * mm});
            skLineSegment(sketch, "E612", {"start": v(-48.5, -67.5) * mm, "end": v(-43.5, -67.5) * mm});
            skLineSegment(sketch, "E613", {"start": v(-43.5, -64.5) * mm, "end": v(-48.5, -64.5) * mm});
            skLineSegment(sketch, "E614", {"start": v(205, 92) * mm, "end": v(205, 80) * mm});
            skLineSegment(sketch, "E615", {"start": v(209, 80) * mm, "end": v(209, 92) * mm});
            skLineSegment(sketch, "E616", {"start": v(193, 92) * mm, "end": v(193, 80) * mm});
            skLineSegment(sketch, "E617", {"start": v(197, 80) * mm, "end": v(197, 92) * mm});
            skLineSegment(sketch, "E618", {"start": v(169, 92) * mm, "end": v(169, 80) * mm});
            skLineSegment(sketch, "E619", {"start": v(173, 80) * mm, "end": v(173, 92) * mm});
            skLineSegment(sketch, "E620", {"start": v(157, 92) * mm, "end": v(157, 80) * mm});
            skLineSegment(sketch, "E621", {"start": v(161, 80) * mm, "end": v(161, 92) * mm});
            skLineSegment(sketch, "E622", {"start": v(145, 92) * mm, "end": v(145, 80) * mm});
            skLineSegment(sketch, "E623", {"start": v(149, 80) * mm, "end": v(149, 92) * mm});
            skLineSegment(sketch, "E624", {"start": v(133, 92) * mm, "end": v(133, 80) * mm});
            skLineSegment(sketch, "E625", {"start": v(137, 80) * mm, "end": v(137, 92) * mm});
            skLineSegment(sketch, "E626", {"start": v(121, 92) * mm, "end": v(121, 80) * mm});
            skLineSegment(sketch, "E627", {"start": v(125, 80) * mm, "end": v(125, 92) * mm});
            skLineSegment(sketch, "E628", {"start": v(-11, 92) * mm, "end": v(-11, 80) * mm});
            skLineSegment(sketch, "E629", {"start": v(-7, 80) * mm, "end": v(-7, 92) * mm});
            skLineSegment(sketch, "E630", {"start": v(-23, 92) * mm, "end": v(-23, 80) * mm});
            skLineSegment(sketch, "E631", {"start": v(-19, 80) * mm, "end": v(-19, 92) * mm});
            skLineSegment(sketch, "E632", {"start": v(-35, 92) * mm, "end": v(-35, 80) * mm});
            skLineSegment(sketch, "E633", {"start": v(-31, 80) * mm, "end": v(-31, 92) * mm});
            skLineSegment(sketch, "E634", {"start": v(-47, 92) * mm, "end": v(-47, 80) * mm});
            skLineSegment(sketch, "E635", {"start": v(-43, 80) * mm, "end": v(-43, 92) * mm});
            skLineSegment(sketch, "E636", {"start": v(-59, 92) * mm, "end": v(-59, 80) * mm});
            skLineSegment(sketch, "E637", {"start": v(-55, 80) * mm, "end": v(-55, 92) * mm});
            skLineSegment(sketch, "E638", {"start": v(-83, 92) * mm, "end": v(-83, 80) * mm});
            skLineSegment(sketch, "E639", {"start": v(-79, 80) * mm, "end": v(-79, 92) * mm});
            skLineSegment(sketch, "E640", {"start": v(-89, 92) * mm, "end": v(-89, 80) * mm});
            skLineSegment(sketch, "E641", {"start": v(-85, 80) * mm, "end": v(-85, 92) * mm});
            skLineSegment(sketch, "E642", {"start": v(-77, 92) * mm, "end": v(-77, 80) * mm});
            skLineSegment(sketch, "E643", {"start": v(-73, 80) * mm, "end": v(-73, 92) * mm});
            skLineSegment(sketch, "E644", {"start": v(-53, 92) * mm, "end": v(-53, 80) * mm});
            skLineSegment(sketch, "E645", {"start": v(-49, 80) * mm, "end": v(-49, 92) * mm});
            skLineSegment(sketch, "E646", {"start": v(-41, 92) * mm, "end": v(-41, 80) * mm});
            skLineSegment(sketch, "E647", {"start": v(-37, 80) * mm, "end": v(-37, 92) * mm});
            skLineSegment(sketch, "E648", {"start": v(-29, 92) * mm, "end": v(-29, 80) * mm});
            skLineSegment(sketch, "E649", {"start": v(-25, 80) * mm, "end": v(-25, 92) * mm});
            skLineSegment(sketch, "E650", {"start": v(-17, 92) * mm, "end": v(-17, 80) * mm});
            skLineSegment(sketch, "E651", {"start": v(-13, 80) * mm, "end": v(-13, 92) * mm});
            skLineSegment(sketch, "E652", {"start": v(-5, 92) * mm, "end": v(-5, 80) * mm});
            skLineSegment(sketch, "E653", {"start": v(-1, 80) * mm, "end": v(-1, 92) * mm});
            skLineSegment(sketch, "E654", {"start": v(127, 92) * mm, "end": v(127, 80) * mm});
            skLineSegment(sketch, "E655", {"start": v(131, 80) * mm, "end": v(131, 92) * mm});
            skLineSegment(sketch, "E656", {"start": v(139, 92) * mm, "end": v(139, 80) * mm});
            skLineSegment(sketch, "E657", {"start": v(143, 80) * mm, "end": v(143, 92) * mm});
            skLineSegment(sketch, "E658", {"start": v(151, 92) * mm, "end": v(151, 80) * mm});
            skLineSegment(sketch, "E659", {"start": v(155, 80) * mm, "end": v(155, 92) * mm});
            skLineSegment(sketch, "E660", {"start": v(163, 92) * mm, "end": v(163, 80) * mm});
            skLineSegment(sketch, "E661", {"start": v(167, 80) * mm, "end": v(167, 92) * mm});
            skLineSegment(sketch, "E662", {"start": v(175, 92) * mm, "end": v(175, 80) * mm});
            skLineSegment(sketch, "E663", {"start": v(179, 80) * mm, "end": v(179, 92) * mm});
            skLineSegment(sketch, "E664", {"start": v(199, 92) * mm, "end": v(199, 80) * mm});
            skLineSegment(sketch, "E665", {"start": v(203, 80) * mm, "end": v(203, 92) * mm});
            skLineSegment(sketch, "E666", {"start": v(-78.5, -67.5) * mm, "end": v(-73.5, -67.5) * mm});
            skLineSegment(sketch, "E667", {"start": v(-73.5, -64.5) * mm, "end": v(-78.5, -64.5) * mm});
            skLineSegment(sketch, "E668", {"start": v(-18.5, -67.5) * mm, "end": v(-13.5, -67.5) * mm});
            skLineSegment(sketch, "E669", {"start": v(-13.5, -64.5) * mm, "end": v(-18.5, -64.5) * mm});
            skLineSegment(sketch, "E670", {"start": v(41.5, -67.5) * mm, "end": v(46.5, -67.5) * mm});
            skLineSegment(sketch, "E671", {"start": v(46.5, -64.5) * mm, "end": v(41.5, -64.5) * mm});
            skLineSegment(sketch, "E672", {"start": v(-48.5, -77.5) * mm, "end": v(-43.5, -77.5) * mm});
            skLineSegment(sketch, "E673", {"start": v(-43.5, -74.5) * mm, "end": v(-48.5, -74.5) * mm});
            skLineSegment(sketch, "E674", {"start": v(11.5, -77.5) * mm, "end": v(16.5, -77.5) * mm});
            skLineSegment(sketch, "E675", {"start": v(16.5, -74.5) * mm, "end": v(11.5, -74.5) * mm});
            skLineSegment(sketch, "E676", {"start": v(191.5, -77.5) * mm, "end": v(196.5, -77.5) * mm});
            skLineSegment(sketch, "E677", {"start": v(196.5, -74.5) * mm, "end": v(191.5, -74.5) * mm});
            skLineSegment(sketch, "E678", {"start": v(-18.5, -87.5) * mm, "end": v(-13.5, -87.5) * mm});
            skLineSegment(sketch, "E679", {"start": v(-13.5, -84.5) * mm, "end": v(-18.5, -84.5) * mm});
            skLineSegment(sketch, "E680", {"start": v(41.5, -87.5) * mm, "end": v(46.5, -87.5) * mm});
            skLineSegment(sketch, "E681", {"start": v(46.5, -84.5) * mm, "end": v(41.5, -84.5) * mm});
            skLineSegment(sketch, "E682", {"start": v(-78.5, -77.5) * mm, "end": v(-73.5, -77.5) * mm});
            skLineSegment(sketch, "E683", {"start": v(-73.5, -74.5) * mm, "end": v(-78.5, -74.5) * mm});
            skArc(sketch, "E684", {"start": v(-73.5, -87.5) * mm, "mid": v(-72, -86) * mm, "end": v(-73.5, -84.5) * mm});
            skArc(sketch, "E685", {"start": v(-78.5, -84.5) * mm, "mid": v(-80, -86) * mm, "end": v(-78.5, -87.5) * mm});
            skArc(sketch, "E686", {"start": v(196.5, -87.5) * mm, "mid": v(198, -86) * mm, "end": v(196.5, -84.5) * mm});
            skArc(sketch, "E687", {"start": v(191.5, -84.5) * mm, "mid": v(190, -86) * mm, "end": v(191.5, -87.5) * mm});
            skArc(sketch, "E688", {"start": v(16.5, -87.5) * mm, "mid": v(18, -86) * mm, "end": v(16.5, -84.5) * mm});
            skArc(sketch, "E689", {"start": v(11.5, -84.5) * mm, "mid": v(10, -86) * mm, "end": v(11.5, -87.5) * mm});
            skArc(sketch, "E690", {"start": v(-43.5, -87.5) * mm, "mid": v(-42, -86) * mm, "end": v(-43.5, -84.5) * mm});
            skArc(sketch, "E691", {"start": v(-48.5, -84.5) * mm, "mid": v(-50, -86) * mm, "end": v(-48.5, -87.5) * mm});
            skArc(sketch, "E692", {"start": v(46.5, -77.5) * mm, "mid": v(48, -76) * mm, "end": v(46.5, -74.5) * mm});
            skArc(sketch, "E693", {"start": v(41.5, -74.5) * mm, "mid": v(40, -76) * mm, "end": v(41.5, -77.5) * mm});
            skArc(sketch, "E694", {"start": v(-13.5, -77.5) * mm, "mid": v(-12, -76) * mm, "end": v(-13.5, -74.5) * mm});
            skArc(sketch, "E695", {"start": v(-18.5, -74.5) * mm, "mid": v(-20, -76) * mm, "end": v(-18.5, -77.5) * mm});
            skArc(sketch, "E696", {"start": v(196.5, -67.5) * mm, "mid": v(198, -66) * mm, "end": v(196.5, -64.5) * mm});
            skArc(sketch, "E697", {"start": v(191.5, -64.5) * mm, "mid": v(190, -66) * mm, "end": v(191.5, -67.5) * mm});
            skArc(sketch, "E698", {"start": v(16.5, -67.5) * mm, "mid": v(18, -66) * mm, "end": v(16.5, -64.5) * mm});
            skArc(sketch, "E699", {"start": v(11.5, -64.5) * mm, "mid": v(10, -66) * mm, "end": v(11.5, -67.5) * mm});
            skArc(sketch, "E700", {"start": v(-43.5, -67.5) * mm, "mid": v(-42, -66) * mm, "end": v(-43.5, -64.5) * mm});
            skArc(sketch, "E701", {"start": v(-48.5, -64.5) * mm, "mid": v(-50, -66) * mm, "end": v(-48.5, -67.5) * mm});
            skArc(sketch, "E702", {"start": v(205, 80) * mm, "mid": v(207, 78) * mm, "end": v(209, 80) * mm});
            skArc(sketch, "E703", {"start": v(209, 92) * mm, "mid": v(207, 94) * mm, "end": v(205, 92) * mm});
            skArc(sketch, "E704", {"start": v(193, 80) * mm, "mid": v(195, 78) * mm, "end": v(197, 80) * mm});
            skArc(sketch, "E705", {"start": v(197, 92) * mm, "mid": v(195, 94) * mm, "end": v(193, 92) * mm});
            skArc(sketch, "E706", {"start": v(169, 80) * mm, "mid": v(171, 78) * mm, "end": v(173, 80) * mm});
            skArc(sketch, "E707", {"start": v(173, 92) * mm, "mid": v(171, 94) * mm, "end": v(169, 92) * mm});
            skArc(sketch, "E708", {"start": v(157, 80) * mm, "mid": v(159, 78) * mm, "end": v(161, 80) * mm});
            skArc(sketch, "E709", {"start": v(161, 92) * mm, "mid": v(159, 94) * mm, "end": v(157, 92) * mm});
            skArc(sketch, "E710", {"start": v(145, 80) * mm, "mid": v(147, 78) * mm, "end": v(149, 80) * mm});
            skArc(sketch, "E711", {"start": v(149, 92) * mm, "mid": v(147, 94) * mm, "end": v(145, 92) * mm});
            skArc(sketch, "E712", {"start": v(133, 80) * mm, "mid": v(135, 78) * mm, "end": v(137, 80) * mm});
            skArc(sketch, "E713", {"start": v(137, 92) * mm, "mid": v(135, 94) * mm, "end": v(133, 92) * mm});
            skArc(sketch, "E714", {"start": v(121, 80) * mm, "mid": v(123, 78) * mm, "end": v(125, 80) * mm});
            skArc(sketch, "E715", {"start": v(125, 92) * mm, "mid": v(123, 94) * mm, "end": v(121, 92) * mm});
            skArc(sketch, "E716", {"start": v(-11, 80) * mm, "mid": v(-9, 78) * mm, "end": v(-7, 80) * mm});
            skArc(sketch, "E717", {"start": v(-7, 92) * mm, "mid": v(-9, 94) * mm, "end": v(-11, 92) * mm});
            skArc(sketch, "E718", {"start": v(-23, 80) * mm, "mid": v(-21, 78) * mm, "end": v(-19, 80) * mm});
            skArc(sketch, "E719", {"start": v(-19, 92) * mm, "mid": v(-21, 94) * mm, "end": v(-23, 92) * mm});
            skArc(sketch, "E720", {"start": v(-35, 80) * mm, "mid": v(-33, 78) * mm, "end": v(-31, 80) * mm});
            skArc(sketch, "E721", {"start": v(-31, 92) * mm, "mid": v(-33, 94) * mm, "end": v(-35, 92) * mm});
            skArc(sketch, "E722", {"start": v(-47, 80) * mm, "mid": v(-45, 78) * mm, "end": v(-43, 80) * mm});
            skArc(sketch, "E723", {"start": v(-43, 92) * mm, "mid": v(-45, 94) * mm, "end": v(-47, 92) * mm});
            skArc(sketch, "E724", {"start": v(-59, 80) * mm, "mid": v(-57, 78) * mm, "end": v(-55, 80) * mm});
            skArc(sketch, "E725", {"start": v(-55, 92) * mm, "mid": v(-57, 94) * mm, "end": v(-59, 92) * mm});
            skArc(sketch, "E726", {"start": v(-83, 80) * mm, "mid": v(-81, 78) * mm, "end": v(-79, 80) * mm});
            skArc(sketch, "E727", {"start": v(-79, 92) * mm, "mid": v(-81, 94) * mm, "end": v(-83, 92) * mm});
            skArc(sketch, "E728", {"start": v(215, -236) * mm, "mid": v(215.7, -235.7) * mm, "end": v(216, -235) * mm});
            skArc(sketch, "E729", {"start": v(-96, -235) * mm, "mid": v(-95.7, -235.7) * mm, "end": v(-95, -236) * mm});
            skArc(sketch, "E730", {"start": v(-95, 96) * mm, "mid": v(-95.7, 95.7) * mm, "end": v(-96, 95) * mm});
            skArc(sketch, "E731", {"start": v(216, 95) * mm, "mid": v(215.7, 95.7) * mm, "end": v(215, 96) * mm});
            skArc(sketch, "E732", {"start": v(-89, 80) * mm, "mid": v(-87, 78) * mm, "end": v(-85, 80) * mm});
            skArc(sketch, "E733", {"start": v(-85, 92) * mm, "mid": v(-87, 94) * mm, "end": v(-89, 92) * mm});
            skArc(sketch, "E734", {"start": v(-77, 80) * mm, "mid": v(-75, 78) * mm, "end": v(-73, 80) * mm});
            skArc(sketch, "E735", {"start": v(-73, 92) * mm, "mid": v(-75, 94) * mm, "end": v(-77, 92) * mm});
            skArc(sketch, "E736", {"start": v(-53, 80) * mm, "mid": v(-51, 78) * mm, "end": v(-49, 80) * mm});
            skArc(sketch, "E737", {"start": v(-49, 92) * mm, "mid": v(-51, 94) * mm, "end": v(-53, 92) * mm});
            skArc(sketch, "E738", {"start": v(-41, 80) * mm, "mid": v(-39, 78) * mm, "end": v(-37, 80) * mm});
            skArc(sketch, "E739", {"start": v(-37, 92) * mm, "mid": v(-39, 94) * mm, "end": v(-41, 92) * mm});
            skArc(sketch, "E740", {"start": v(-29, 80) * mm, "mid": v(-27, 78) * mm, "end": v(-25, 80) * mm});
            skArc(sketch, "E741", {"start": v(-25, 92) * mm, "mid": v(-27, 94) * mm, "end": v(-29, 92) * mm});
            skArc(sketch, "E742", {"start": v(-17, 80) * mm, "mid": v(-15, 78) * mm, "end": v(-13, 80) * mm});
            skArc(sketch, "E743", {"start": v(-13, 92) * mm, "mid": v(-15, 94) * mm, "end": v(-17, 92) * mm});
            skArc(sketch, "E744", {"start": v(-5, 80) * mm, "mid": v(-3, 78) * mm, "end": v(-1, 80) * mm});
            skArc(sketch, "E745", {"start": v(-1, 92) * mm, "mid": v(-3, 94) * mm, "end": v(-5, 92) * mm});
            skArc(sketch, "E746", {"start": v(127, 80) * mm, "mid": v(129, 78) * mm, "end": v(131, 80) * mm});
            skArc(sketch, "E747", {"start": v(131, 92) * mm, "mid": v(129, 94) * mm, "end": v(127, 92) * mm});
            skArc(sketch, "E748", {"start": v(139, 80) * mm, "mid": v(141, 78) * mm, "end": v(143, 80) * mm});
            skArc(sketch, "E749", {"start": v(143, 92) * mm, "mid": v(141, 94) * mm, "end": v(139, 92) * mm});
            skArc(sketch, "E750", {"start": v(151, 80) * mm, "mid": v(153, 78) * mm, "end": v(155, 80) * mm});
            skArc(sketch, "E751", {"start": v(155, 92) * mm, "mid": v(153, 94) * mm, "end": v(151, 92) * mm});
            skArc(sketch, "E752", {"start": v(163, 80) * mm, "mid": v(165, 78) * mm, "end": v(167, 80) * mm});
            skArc(sketch, "E753", {"start": v(167, 92) * mm, "mid": v(165, 94) * mm, "end": v(163, 92) * mm});
            skArc(sketch, "E754", {"start": v(175, 80) * mm, "mid": v(177, 78) * mm, "end": v(179, 80) * mm});
            skArc(sketch, "E755", {"start": v(179, 92) * mm, "mid": v(177, 94) * mm, "end": v(175, 92) * mm});
            skArc(sketch, "E756", {"start": v(199, 80) * mm, "mid": v(201, 78) * mm, "end": v(203, 80) * mm});
            skArc(sketch, "E757", {"start": v(203, 92) * mm, "mid": v(201, 94) * mm, "end": v(199, 92) * mm});
            skArc(sketch, "E758", {"start": v(-73.5, -67.5) * mm, "mid": v(-72, -66) * mm, "end": v(-73.5, -64.5) * mm});
            skArc(sketch, "E759", {"start": v(-78.5, -64.5) * mm, "mid": v(-80, -66) * mm, "end": v(-78.5, -67.5) * mm});
            skArc(sketch, "E760", {"start": v(-13.5, -67.5) * mm, "mid": v(-12, -66) * mm, "end": v(-13.5, -64.5) * mm});
            skArc(sketch, "E761", {"start": v(-18.5, -64.5) * mm, "mid": v(-20, -66) * mm, "end": v(-18.5, -67.5) * mm});
            skArc(sketch, "E762", {"start": v(46.5, -67.5) * mm, "mid": v(48, -66) * mm, "end": v(46.5, -64.5) * mm});
            skArc(sketch, "E763", {"start": v(41.5, -64.5) * mm, "mid": v(40, -66) * mm, "end": v(41.5, -67.5) * mm});
            skArc(sketch, "E764", {"start": v(-43.5, -77.5) * mm, "mid": v(-42, -76) * mm, "end": v(-43.5, -74.5) * mm});
            skArc(sketch, "E765", {"start": v(-48.5, -74.5) * mm, "mid": v(-50, -76) * mm, "end": v(-48.5, -77.5) * mm});
            skArc(sketch, "E766", {"start": v(16.5, -77.5) * mm, "mid": v(18, -76) * mm, "end": v(16.5, -74.5) * mm});
            skArc(sketch, "E767", {"start": v(11.5, -74.5) * mm, "mid": v(10, -76) * mm, "end": v(11.5, -77.5) * mm});
            skArc(sketch, "E768", {"start": v(196.5, -77.5) * mm, "mid": v(198, -76) * mm, "end": v(196.5, -74.5) * mm});
            skArc(sketch, "E769", {"start": v(191.5, -74.5) * mm, "mid": v(190, -76) * mm, "end": v(191.5, -77.5) * mm});
            skArc(sketch, "E770", {"start": v(-13.5, -87.5) * mm, "mid": v(-12, -86) * mm, "end": v(-13.5, -84.5) * mm});
            skArc(sketch, "E771", {"start": v(-18.5, -84.5) * mm, "mid": v(-20, -86) * mm, "end": v(-18.5, -87.5) * mm});
            skArc(sketch, "E772", {"start": v(46.5, -87.5) * mm, "mid": v(48, -86) * mm, "end": v(46.5, -84.5) * mm});
            skArc(sketch, "E773", {"start": v(41.5, -84.5) * mm, "mid": v(40, -86) * mm, "end": v(41.5, -87.5) * mm});
            skArc(sketch, "E774", {"start": v(-73.5, -77.5) * mm, "mid": v(-72, -76) * mm, "end": v(-73.5, -74.5) * mm});
            skArc(sketch, "E775", {"start": v(-78.5, -74.5) * mm, "mid": v(-80, -76) * mm, "end": v(-78.5, -77.5) * mm});
            skLineSegment(sketch, "E776", {"start": v(-96, 95) * mm, "end": v(-96, -235) * mm});
            skLineSegment(sketch, "E777", {"start": v(-95, -236) * mm, "end": v(215, -236) * mm});
            skLineSegment(sketch, "E778", {"start": v(216, -235) * mm, "end": v(216, 95) * mm});
            skLineSegment(sketch, "E779", {"start": v(215, 96) * mm, "end": v(-95, 96) * mm});
            skSolve(sketch);
        }
        {
            var Q0;
            Q0=makeQuery(id+"F23.imprint","IMPRINT",FACE,{"disambiguationData":[TD([[makeQuery(id+"F23.imprint","IMPRINT",EDGE,{"derivedFrom":sQuery(id+"F23.wireOp",EDGE,"E560")}),1.0]])]});
            extrude(context, id + "F24", {"entities" : qUnion([Q0]), "depth" : 2 * mm});
        }
        {
            var Q0;
            Q0=qCreatedBy(makeId("Top.planeOp"),FACE);
            var sketch = newSketch(context, id + "F25", { "sketchPlane" : qUnion([Q0])});
            skCircle(sketch, "E780", {"center": v(-93, 55.5) * mm, "radius": 1.5 * mm});
            skCircle(sketch, "E781", {"center": v(213, -209.5) * mm, "radius": 1.5 * mm});
            skCircle(sketch, "E782", {"center": v(-93, -209.5) * mm, "radius": 1.5 * mm});
            skCircle(sketch, "E783", {"center": v(213, 55.5) * mm, "radius": 1.5 * mm});
            skLineSegment(sketch, "E784", {"start": v(64.5, 70) * mm, "end": v(55.5, 70) * mm});
            skLineSegment(sketch, "E785", {"start": v(64.5, 71.5) * mm, "end": v(64.5, 70) * mm});
            skLineSegment(sketch, "E786", {"start": v(55.5, 70) * mm, "end": v(55.5, 71.5) * mm});
            skArc(sketch, "E787", {"start": v(65.5, 72.5) * mm, "mid": v(64.8, 72.2) * mm, "end": v(64.5, 71.5) * mm});
            skArc(sketch, "E788", {"start": v(216, 71.5) * mm, "mid": v(215.7, 72.2) * mm, "end": v(215, 72.5) * mm});
            skArc(sketch, "E789", {"start": v(215, -212.5) * mm, "mid": v(215.7, -212.2) * mm, "end": v(216, -211.5) * mm});
            skArc(sketch, "E790", {"start": v(-96, -211.5) * mm, "mid": v(-95.7, -212.2) * mm, "end": v(-95, -212.5) * mm});
            skArc(sketch, "E791", {"start": v(-95, 72.5) * mm, "mid": v(-95.7, 72.2) * mm, "end": v(-96, 71.5) * mm});
            skArc(sketch, "E792", {"start": v(55.5, 71.5) * mm, "mid": v(55.2, 72.2) * mm, "end": v(54.5, 72.5) * mm});
            skLineSegment(sketch, "E793", {"start": v(-95, 72.5) * mm, "end": v(54.5, 72.5) * mm});
            skLineSegment(sketch, "E794", {"start": v(65.5, 72.5) * mm, "end": v(215, 72.5) * mm});
            skLineSegment(sketch, "E795", {"start": v(216, 71.5) * mm, "end": v(216, -211.5) * mm});
            skLineSegment(sketch, "E796", {"start": v(215, -212.5) * mm, "end": v(-95, -212.5) * mm});
            skLineSegment(sketch, "E797", {"start": v(-96, -211.5) * mm, "end": v(-96, 71.5) * mm});
            skSolve(sketch);
        }
        {
            var Q0;
            Q0=makeQuery(id+"F25.imprint","IMPRINT",FACE,{"disambiguationData":[TD([[makeQuery(id+"F25.imprint","IMPRINT",EDGE,{"derivedFrom":sQuery(id+"F25.wireOp",EDGE,"E780")}),1.0]])]});
            extrude(context, id + "F26", {"entities" : qUnion([Q0]), "depth" : 2 * mm});
        }
        {
            var Q0;
            Q0=makeQuery(id+"F20.imprint","IMPRINT",FACE,{"disambiguationData":[TD([[makeQuery(id+"F20.imprint","IMPRINT",EDGE,{"derivedFrom":sQuery(id+"F20.wireOp",EDGE,"E549.bottom")}),1.0]])]});
            extrude(context, id + "F27", {"entities" : qUnion([Q0]), "depth" : 4 * mm});
        }
    });
